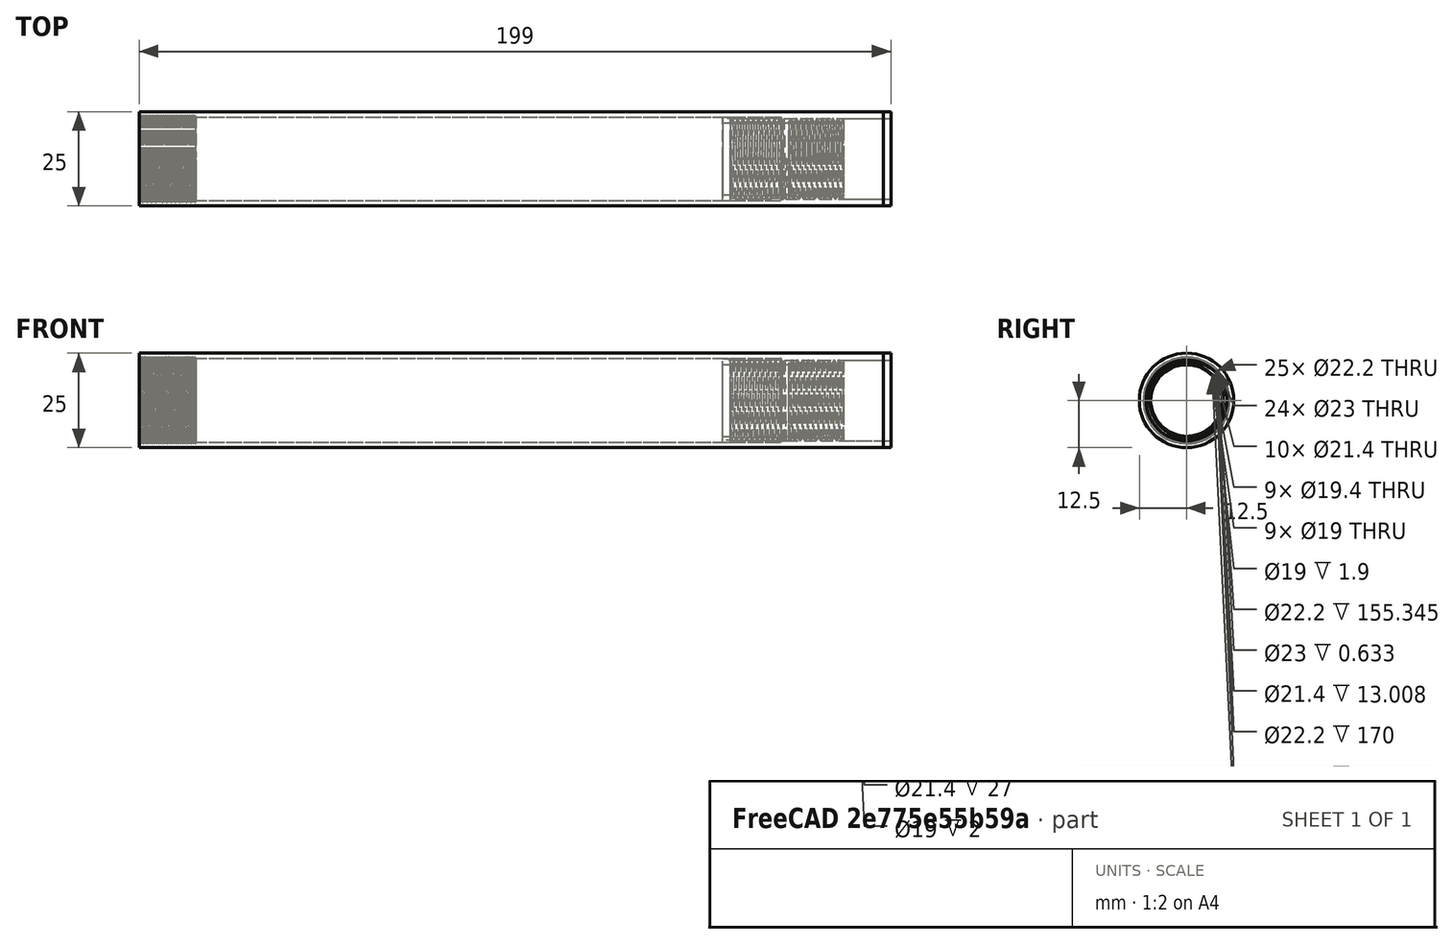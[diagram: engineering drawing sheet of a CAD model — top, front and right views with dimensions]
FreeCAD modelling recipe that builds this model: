
FCSTD DOCUMENT  (FreeCAD 0.17R13541 (Git))
Label: ERG-T-01-BH-02
License: All rights reserved
LicenseURL: http://en.wikipedia.org/wiki/All_rights_reserved
objects: Drawing::FeatureViewPython×76, Part::Cylinder×18, Part::Cut×12, Drawing::FeatureViewPart×8, Part::MultiFuse×8, Drawing::FeaturePage×4, Sketcher::SketchObject×4, Part::Helix×4, Part::Sweep×4, Part::Feature×2
note: 52 computed .brp shape members not serialized (recipe doc carries the construction recipe); baked Part::Feature solids carry a one-line shape summary decoded from their .brp

FEATURE [Drawing::FeatureViewPython] dim130  # drawing view (typed FeaturePython)
  Rotation = 0
  ViewResult = <g> \n  <line x1="95.000000" y1="103.600000" x2="95.000000" y2="144.306302" style="stroke:rgb(255,0,0);stroke-width:0.10" />\n<line x1="47.000000" y1="102.500000" x2="47.000000" y2="144.306302" style="stroke:rgb(255,0,0);stroke-width:0.10" />\n<line x1="95.000000" y1="143.306302" x2="47.000000" y2="143.306302" style="stroke:rgb(255,0,0);stroke-width:0.10" /> \n  <polygon points="47.000000,143.306302 49.000000,143.806302 49.500000,143.306302 49.000000,142.806302" style="fill:rgb(255,0,0);stroke:rgb(255,0,0);stroke-width:0" /><polygon points="95.000000,143.306302 93.000000,142.806302 92.500000,143.306302 93.000000,143.806302" style="fill:rgb(255,0,0);stroke:rgb(255,0,0);stroke-width:0" /> \n  <text x="71.000000" y="141.306302" font-family="inherit" font-size="3.6" fill="rgb(0,0,0)" text-anchor="middle" transform="rotate(0.000000 71.000000,141.306302)" >24</text> </g>
  Visible = false
  X = 0
  Y = 0
  arrowL1 = 2
  arrowL2 = 0.5
  arrowW = 1
  arrow_scheme = 0
  autoPlaceOffset = 2
  autoPlaceText = true
  click1_x = 59.2162
  click1_y = 143.306
  click2_x = 59.2162
  click2_y = 143.306
  comma_decimal_place = false
  dimension_line_overshoot = 1
  gap_datum_points = 0
  halfDimension_linear = false
  lineColor = rgb(255,0,0)
  strokeWidth = 0.1
  textFormat_linear = %(value)3.3f
  textRenderer_color = rgb(0,0,0)
  textRenderer_family = inherit
  textRenderer_size = 3.6
  unit_custom_scale = 1.7
  unit_scheme = 0
FEATURE [Drawing::FeatureViewPython] dim131  # drawing view (typed FeaturePython)
  Rotation = 0
  ViewResult = <g> \n  <line x1="95.000000" y1="103.600000" x2="95.000000" y2="144.274206" style="stroke:rgb(255,0,0);stroke-width:0.10" />\n<line x1="250.000000" y1="106.500000" x2="250.000000" y2="144.274206" style="stroke:rgb(255,0,0);stroke-width:0.10" />\n<line x1="95.000000" y1="143.274206" x2="250.000000" y2="143.274206" style="stroke:rgb(255,0,0);stroke-width:0.10" /> \n  <polygon points="250.000000,143.274206 248.000000,142.774206 247.500000,143.274206 248.000000,143.774206" style="fill:rgb(255,0,0);stroke:rgb(255,0,0);stroke-width:0" /><polygon points="95.000000,143.274206 97.000000,143.774206 97.500000,143.274206 97.000000,142.774206" style="fill:rgb(255,0,0);stroke:rgb(255,0,0);stroke-width:0" /> \n  <text x="172.500000" y="141.274206" font-family="inherit" font-size="3.6" fill="rgb(0,0,0)" text-anchor="middle" transform="rotate(0.000000 172.500000,141.274206)" >77.5</text> </g>
  Visible = false
  X = 0
  Y = 0
  arrowL1 = 2
  arrowL2 = 0.5
  arrowW = 1
  arrow_scheme = 0
  autoPlaceOffset = 2
  autoPlaceText = true
  click1_x = 247.264
  click1_y = 143.274
  click2_x = 247.264
  click2_y = 143.274
  comma_decimal_place = false
  dimension_line_overshoot = 1
  gap_datum_points = 0
  halfDimension_linear = false
  lineColor = rgb(255,0,0)
  strokeWidth = 0.1
  textFormat_linear = %(value)3.3f
  textRenderer_color = rgb(0,0,0)
  textRenderer_family = inherit
  textRenderer_size = 3.6
  unit_custom_scale = 1.7
  unit_scheme = 0
FEATURE [Drawing::FeatureViewPython] dim132  # drawing view (typed FeaturePython)
  Rotation = 0
  ViewResult = <g> \n  <line x1="95.000000" y1="100.500000" x2="95.000000" y2="91.946246" style="stroke:rgb(255,0,0);stroke-width:0.10" />\n<line x1="91.000000" y1="100.500000" x2="91.000000" y2="91.946246" style="stroke:rgb(255,0,0);stroke-width:0.10" />\n<line x1="95.000000" y1="92.946246" x2="91.000000" y2="92.946246" style="stroke:rgb(255,0,0);stroke-width:0.10" /> \n  <polygon points="91.000000,92.946246 89.000000,92.446246 88.500000,92.946246 89.000000,93.446246" style="fill:rgb(255,0,0);stroke:rgb(255,0,0);stroke-width:0" /><polygon points="95.000000,92.946246 97.000000,93.446246 97.500000,92.946246 97.000000,92.446246" style="fill:rgb(255,0,0);stroke:rgb(255,0,0);stroke-width:0" /> \n  <text x="93.000000" y="90.946246" font-family="inherit" font-size="3.6" fill="rgb(0,0,0)" text-anchor="middle" transform="rotate(0.000000 93.000000,90.946246)" >2</text> </g>
  Visible = false
  X = 0
  Y = 0
  arrowL1 = 2
  arrowL2 = 0.5
  arrowW = 1
  arrow_scheme = 0
  autoPlaceOffset = 2
  autoPlaceText = true
  click1_x = 91.8628
  click1_y = 92.9462
  click2_x = 91.8628
  click2_y = 92.9462
  comma_decimal_place = false
  dimension_line_overshoot = 1
  gap_datum_points = 0
  halfDimension_linear = false
  lineColor = rgb(255,0,0)
  strokeWidth = 0.1
  textFormat_linear = %(value)3.3f
  textRenderer_color = rgb(0,0,0)
  textRenderer_family = inherit
  textRenderer_size = 3.6
  unit_custom_scale = 1.7
  unit_scheme = 0
FEATURE [Drawing::FeatureViewPython] dim133  # drawing view (typed FeaturePython)
  Rotation = 0
  ViewResult = <g> \n  <line x1="62.208000" y1="60.500000" x2="62.208000" y2="72.297691" style="stroke:rgb(255,0,0);stroke-width:0.10" />\n<line x1="91.000000" y1="62.500000" x2="91.000000" y2="72.297691" style="stroke:rgb(255,0,0);stroke-width:0.10" />\n<line x1="62.208000" y1="71.297691" x2="91.000000" y2="71.297691" style="stroke:rgb(255,0,0);stroke-width:0.10" /> \n  <polygon points="91.000000,71.297691 89.000000,70.797691 88.500000,71.297691 89.000000,71.797691" style="fill:rgb(255,0,0);stroke:rgb(255,0,0);stroke-width:0" /><polygon points="62.208000,71.297691 64.208000,71.797691 64.708000,71.297691 64.208000,70.797691" style="fill:rgb(255,0,0);stroke:rgb(255,0,0);stroke-width:0" /> \n  <text x="76.604000" y="69.297691" font-family="inherit" font-size="3.6" fill="rgb(0,0,0)" text-anchor="middle" transform="rotate(0.000000 76.604000,69.297691)" >14.2</text> </g>
  Visible = false
  X = 0
  Y = 0
  arrowL1 = 2
  arrowL2 = 0.5
  arrowW = 1
  arrow_scheme = 0
  autoPlaceOffset = 2
  autoPlaceText = true
  click1_x = 89.6096
  click1_y = 71.2977
  click2_x = 89.6096
  click2_y = 71.2977
  comma_decimal_place = false
  dimension_line_overshoot = 1
  gap_datum_points = 0
  halfDimension_linear = false
  lineColor = rgb(255,0,0)
  strokeWidth = 0.1
  textFormat_linear = 14.2
  textRenderer_color = rgb(0,0,0)
  textRenderer_family = inherit
  textRenderer_size = 3.6
  unit_custom_scale = 1.7
  unit_scheme = 0
FEATURE [Drawing::FeatureViewPython] dim134  # drawing view (typed FeaturePython)
  Rotation = 0
  ViewResult = <g> \n  <line x1="47.000000" y1="60.500000" x2="47.000000" y2="72.294300" style="stroke:rgb(255,0,0);stroke-width:0.10" />\n<line x1="62.208000" y1="60.500000" x2="62.208000" y2="72.294300" style="stroke:rgb(255,0,0);stroke-width:0.10" />\n<line x1="47.000000" y1="71.294300" x2="62.208000" y2="71.294300" style="stroke:rgb(255,0,0);stroke-width:0.10" /> \n  <polygon points="62.208000,71.294300 60.208000,70.794300 59.708000,71.294300 60.208000,71.794300" style="fill:rgb(255,0,0);stroke:rgb(255,0,0);stroke-width:0" /><polygon points="47.000000,71.294300 49.000000,71.794300 49.500000,71.294300 49.000000,70.794300" style="fill:rgb(255,0,0);stroke:rgb(255,0,0);stroke-width:0" /> \n  <text x="54.604000" y="69.294300" font-family="inherit" font-size="3.6" fill="rgb(0,0,0)" text-anchor="middle" transform="rotate(0.000000 54.604000,69.294300)" >7.8</text> </g>
  Visible = false
  X = 0
  Y = 0
  arrowL1 = 2
  arrowL2 = 0.5
  arrowW = 1
  arrow_scheme = 0
  autoPlaceOffset = 2
  autoPlaceText = true
  click1_x = 60.9176
  click1_y = 71.2943
  click2_x = 60.9176
  click2_y = 71.2943
  comma_decimal_place = false
  dimension_line_overshoot = 1
  gap_datum_points = 0
  halfDimension_linear = false
  lineColor = rgb(255,0,0)
  strokeWidth = 0.1
  textFormat_linear = 7.8
  textRenderer_color = rgb(0,0,0)
  textRenderer_family = inherit
  textRenderer_size = 3.6
  unit_custom_scale = 1.7
  unit_scheme = 0
FEATURE [Drawing::FeatureViewPython] dim160  # drawing view (typed FeaturePython)
  Rotation = 0
  ViewResult = <g> \n  <line x1="250.000000" y1="59.400000" x2="266.991260" y2="59.400000" style="stroke:rgb(255,0,0);stroke-width:0.10" />\n<line x1="250.000000" y1="56.500000" x2="266.991260" y2="56.500000" style="stroke:rgb(255,0,0);stroke-width:0.10" />\n<line x1="265.991260" y1="59.400000" x2="265.991260" y2="56.500000" style="stroke:rgb(255,0,0);stroke-width:0.10" /> \n  <polygon points="265.991260,56.500000 266.491260,54.500000 265.991260,54.000000 265.491260,54.500000" style="fill:rgb(255,0,0);stroke:rgb(255,0,0);stroke-width:0" /><polygon points="265.991260,59.400000 265.491260,61.400000 265.991260,61.900000 266.491260,61.400000" style="fill:rgb(255,0,0);stroke:rgb(255,0,0);stroke-width:0" /> \n  <text x="263.991260" y="57.950000" font-family="inherit" font-size="3.6" fill="rgb(0,0,0)" text-anchor="middle" transform="rotate(-90.000000 263.991260,57.950000)" >1.45</text> </g>
  Visible = false
  X = 0
  Y = 0
  arrowL1 = 2
  arrowL2 = 0.5
  arrowW = 1
  arrow_scheme = 0
  autoPlaceOffset = 2
  autoPlaceText = true
  click1_x = 265.991
  click1_y = 61.2489
  click2_x = 265.991
  click2_y = 61.2489
  comma_decimal_place = false
  dimension_line_overshoot = 1
  gap_datum_points = 0
  halfDimension_linear = false
  lineColor = rgb(255,0,0)
  strokeWidth = 0.1
  textFormat_linear = %(value)3.3f
  textRenderer_color = rgb(0,0,0)
  textRenderer_family = inherit
  textRenderer_size = 3.6
  unit_custom_scale = 1.7
  unit_scheme = 0
FEATURE [Drawing::FeatureViewPython] dim161  # drawing view (typed FeaturePython)
  Rotation = 0
  ViewResult = <g> \n  <line x1="250.000000" y1="59.400000" x2="266.857529" y2="59.400000" style="stroke:rgb(255,0,0);stroke-width:0.10" />\n<line x1="250.000000" y1="103.600000" x2="266.857529" y2="103.600000" style="stroke:rgb(255,0,0);stroke-width:0.10" />\n<line x1="265.857529" y1="59.400000" x2="265.857529" y2="103.600000" style="stroke:rgb(255,0,0);stroke-width:0.10" /> \n  <polygon points="265.857529,103.600000 266.357529,101.600000 265.857529,101.100000 265.357529,101.600000" style="fill:rgb(255,0,0);stroke:rgb(255,0,0);stroke-width:0" /><polygon points="265.857529,59.400000 265.357529,61.400000 265.857529,61.900000 266.357529,61.400000" style="fill:rgb(255,0,0);stroke:rgb(255,0,0);stroke-width:0" /> \n  <text x="263.857529" y="81.500000" font-family="inherit" font-size="3.6" fill="rgb(0,0,0)" text-anchor="middle" transform="rotate(-90.000000 263.857529,81.500000)" >22.1</text> </g>
  Visible = false
  X = 0
  Y = 0
  arrowL1 = 2
  arrowL2 = 0.5
  arrowW = 1
  arrow_scheme = 0
  autoPlaceOffset = 2
  autoPlaceText = true
  click1_x = 265.858
  click1_y = 102.973
  click2_x = 265.858
  click2_y = 102.973
  comma_decimal_place = false
  dimension_line_overshoot = 1
  gap_datum_points = 0
  halfDimension_linear = false
  lineColor = rgb(255,0,0)
  strokeWidth = 0.1
  textFormat_linear = %(value)3.3f
  textRenderer_color = rgb(0,0,0)
  textRenderer_family = inherit
  textRenderer_size = 3.6
  unit_custom_scale = 1.7
  unit_scheme = 0
FEATURE [Drawing::FeatureViewPython] dim162  # drawing view (typed FeaturePython)
  Rotation = 0
  ViewResult = <g> \n  <line x1="250.000000" y1="106.500000" x2="266.857529" y2="106.500000" style="stroke:rgb(255,0,0);stroke-width:0.10" />\n<line x1="250.000000" y1="103.600000" x2="266.857529" y2="103.600000" style="stroke:rgb(255,0,0);stroke-width:0.10" />\n<line x1="265.857529" y1="106.500000" x2="265.857529" y2="103.600000" style="stroke:rgb(255,0,0);stroke-width:0.10" /> \n  <polygon points="265.857529,103.600000 266.357529,101.600000 265.857529,101.100000 265.357529,101.600000" style="fill:rgb(255,0,0);stroke:rgb(255,0,0);stroke-width:0" /><polygon points="265.857529,106.500000 265.357529,108.500000 265.857529,109.000000 266.357529,108.500000" style="fill:rgb(255,0,0);stroke:rgb(255,0,0);stroke-width:0" /> \n  <text x="263.857529" y="105.050000" font-family="inherit" font-size="3.6" fill="rgb(0,0,0)" text-anchor="middle" transform="rotate(-90.000000 263.857529,105.050000)" >1.45</text> </g>
  Visible = false
  X = 0
  Y = 0
  arrowL1 = 2
  arrowL2 = 0.5
  arrowW = 1
  arrow_scheme = 0
  autoPlaceOffset = 2
  autoPlaceText = true
  click1_x = 265.858
  click1_y = 105.915
  click2_x = 265.858
  click2_y = 105.915
  comma_decimal_place = false
  dimension_line_overshoot = 1
  gap_datum_points = 0
  halfDimension_linear = false
  lineColor = rgb(255,0,0)
  strokeWidth = 0.1
  textFormat_linear = %(value)3.3f
  textRenderer_color = rgb(0,0,0)
  textRenderer_family = inherit
  textRenderer_size = 3.6
  unit_custom_scale = 1.7
  unit_scheme = 0
FEATURE [Drawing::FeatureViewPython] dim140  # drawing view (typed FeaturePython)
  Rotation = 0
  ViewResult = <g> \n  <line x1="95.000000" y1="62.500000" x2="113.045957" y2="62.500000" style="stroke:rgb(255,0,0);stroke-width:0.10" />\n<line x1="95.000000" y1="100.500000" x2="113.045957" y2="100.500000" style="stroke:rgb(255,0,0);stroke-width:0.10" />\n<line x1="112.045957" y1="62.500000" x2="112.045957" y2="100.500000" style="stroke:rgb(255,0,0);stroke-width:0.10" /> \n  <polygon points="112.045957,100.500000 112.545957,98.500000 112.045957,98.000000 111.545957,98.500000" style="fill:rgb(255,0,0);stroke:rgb(255,0,0);stroke-width:0" /><polygon points="112.045957,62.500000 111.545957,64.500000 112.045957,65.000000 112.545957,64.500000" style="fill:rgb(255,0,0);stroke:rgb(255,0,0);stroke-width:0" /> \n  <text x="110.045957" y="81.500000" font-family="inherit" font-size="3.6" fill="rgb(0,0,0)" text-anchor="middle" transform="rotate(-90.000000 110.045957,81.500000)" >19</text> </g>
  Visible = false
  X = 0
  Y = 0
  arrowL1 = 2
  arrowL2 = 0.5
  arrowW = 1
  arrow_scheme = 0
  autoPlaceOffset = 2
  autoPlaceText = true
  click1_x = 112.046
  click1_y = 100.247
  click2_x = 112.046
  click2_y = 100.247
  comma_decimal_place = false
  dimension_line_overshoot = 1
  gap_datum_points = 0
  halfDimension_linear = false
  lineColor = rgb(255,0,0)
  strokeWidth = 0.1
  textFormat_linear = %(value)3.3f
  textRenderer_color = rgb(0,0,0)
  textRenderer_family = inherit
  textRenderer_size = 3.6
  unit_custom_scale = 1.7
  unit_scheme = 0
FEATURE [Drawing::FeatureViewPython] dim135  # drawing view (typed FeaturePython)
  Rotation = 0
  ViewResult = <g> \n  <line x1="91.000000" y1="100.500000" x2="91.000000" y2="92.012785" style="stroke:rgb(255,0,0);stroke-width:0.10" />\n<line x1="47.000000" y1="102.500000" x2="47.000000" y2="92.012785" style="stroke:rgb(255,0,0);stroke-width:0.10" />\n<line x1="91.000000" y1="93.012785" x2="47.000000" y2="93.012785" style="stroke:rgb(255,0,0);stroke-width:0.10" /> \n  <polygon points="47.000000,93.012785 49.000000,93.512785 49.500000,93.012785 49.000000,92.512785" style="fill:rgb(255,0,0);stroke:rgb(255,0,0);stroke-width:0" /><polygon points="91.000000,93.012785 89.000000,92.512785 88.500000,93.012785 89.000000,93.512785" style="fill:rgb(255,0,0);stroke:rgb(255,0,0);stroke-width:0" /> \n  <text x="69.000000" y="91.012785" font-family="inherit" font-size="3.6" fill="rgb(0,0,0)" text-anchor="middle" transform="rotate(0.000000 69.000000,91.012785)" >22</text> </g>
  Visible = false
  X = 0
  Y = 0
  arrowL1 = 2
  arrowL2 = 0.5
  arrowW = 1
  arrow_scheme = 0
  autoPlaceOffset = 2
  autoPlaceText = true
  click1_x = 47.2505
  click1_y = 93.0128
  click2_x = 47.2505
  click2_y = 93.0128
  comma_decimal_place = false
  dimension_line_overshoot = 1
  gap_datum_points = 0
  halfDimension_linear = false
  lineColor = rgb(255,0,0)
  strokeWidth = 0.1
  textFormat_linear = %(value)3.3f
  textRenderer_color = rgb(0,0,0)
  textRenderer_family = inherit
  textRenderer_size = 3.6
  unit_custom_scale = 1.7
  unit_scheme = 0
FEATURE [Drawing::FeatureViewPython] dim136  # drawing view (typed FeaturePython)
  Rotation = 0
  ViewResult = <g> \n  <line x1="47.000000" y1="60.500000" x2="41.165796" y2="60.500000" style="stroke:rgb(255,0,0);stroke-width:0.10" />\n<line x1="47.000000" y1="56.500000" x2="41.165796" y2="56.500000" style="stroke:rgb(255,0,0);stroke-width:0.10" />\n<line x1="42.165796" y1="60.500000" x2="42.165796" y2="56.500000" style="stroke:rgb(255,0,0);stroke-width:0.10" /> \n  <polygon points="42.165796,56.500000 42.665796,54.500000 42.165796,54.000000 41.665796,54.500000" style="fill:rgb(255,0,0);stroke:rgb(255,0,0);stroke-width:0" /><polygon points="42.165796,60.500000 41.665796,62.500000 42.165796,63.000000 42.665796,62.500000" style="fill:rgb(255,0,0);stroke:rgb(255,0,0);stroke-width:0" /> \n  <text x="40.165796" y="58.500000" font-family="inherit" font-size="3.6" fill="rgb(0,0,0)" text-anchor="middle" transform="rotate(-90.000000 40.165796,58.500000)" >2</text> </g>
  Visible = false
  X = 0
  Y = 0
  arrowL1 = 2
  arrowL2 = 0.5
  arrowW = 1
  arrow_scheme = 0
  autoPlaceOffset = 2
  autoPlaceText = true
  click1_x = 42.1658
  click1_y = 59.7762
  click2_x = 42.1658
  click2_y = 59.7762
  comma_decimal_place = false
  dimension_line_overshoot = 1
  gap_datum_points = 0
  halfDimension_linear = false
  lineColor = rgb(255,0,0)
  strokeWidth = 0.1
  textFormat_linear = %(value)3.3f
  textRenderer_color = rgb(0,0,0)
  textRenderer_family = inherit
  textRenderer_size = 3.6
  unit_custom_scale = 1.7
  unit_scheme = 0
FEATURE [Drawing::FeatureViewPython] dim137  # drawing view (typed FeaturePython)
  Rotation = 0
  ViewResult = <g> \n  <line x1="47.000000" y1="106.500000" x2="41.289813" y2="106.500000" style="stroke:rgb(255,0,0);stroke-width:0.10" />\n<line x1="47.000000" y1="102.500000" x2="41.289813" y2="102.500000" style="stroke:rgb(255,0,0);stroke-width:0.10" />\n<line x1="42.289813" y1="106.500000" x2="42.289813" y2="102.500000" style="stroke:rgb(255,0,0);stroke-width:0.10" /> \n  <polygon points="42.289813,102.500000 42.789813,100.500000 42.289813,100.000000 41.789813,100.500000" style="fill:rgb(255,0,0);stroke:rgb(255,0,0);stroke-width:0" /><polygon points="42.289813,106.500000 41.789813,108.500000 42.289813,109.000000 42.789813,108.500000" style="fill:rgb(255,0,0);stroke:rgb(255,0,0);stroke-width:0" /> \n  <text x="40.289813" y="104.500000" font-family="inherit" font-size="3.6" fill="rgb(0,0,0)" text-anchor="middle" transform="rotate(-90.000000 40.289813,104.500000)" >2</text> </g>
  Visible = false
  X = 0
  Y = 0
  arrowL1 = 2
  arrowL2 = 0.5
  arrowW = 1
  arrow_scheme = 0
  autoPlaceOffset = 2
  autoPlaceText = true
  click1_x = 42.2898
  click1_y = 105.042
  click2_x = 42.2898
  click2_y = 105.042
  comma_decimal_place = false
  dimension_line_overshoot = 1
  gap_datum_points = 0
  halfDimension_linear = false
  lineColor = rgb(255,0,0)
  strokeWidth = 0.1
  textFormat_linear = %(value)3.3f
  textRenderer_color = rgb(0,0,0)
  textRenderer_family = inherit
  textRenderer_size = 3.6
  unit_custom_scale = 1.7
  unit_scheme = 0
FEATURE [Drawing::FeatureViewPython] dim138  # drawing view (typed FeaturePython)
  Rotation = 0
  ViewResult = <g> \n  <line x1="47.000000" y1="60.500000" x2="41.372491" y2="60.500000" style="stroke:rgb(255,0,0);stroke-width:0.10" />\n<line x1="47.000000" y1="102.500000" x2="41.372491" y2="102.500000" style="stroke:rgb(255,0,0);stroke-width:0.10" />\n<line x1="42.372491" y1="60.500000" x2="42.372491" y2="102.500000" style="stroke:rgb(255,0,0);stroke-width:0.10" /> \n  <polygon points="42.372491,102.500000 42.872491,100.500000 42.372491,100.000000 41.872491,100.500000" style="fill:rgb(255,0,0);stroke:rgb(255,0,0);stroke-width:0" /><polygon points="42.372491,60.500000 41.872491,62.500000 42.372491,63.000000 42.872491,62.500000" style="fill:rgb(255,0,0);stroke:rgb(255,0,0);stroke-width:0" /> \n  <text x="40.372491" y="81.500000" font-family="inherit" font-size="3.6" fill="rgb(0,0,0)" text-anchor="middle" transform="rotate(-90.000000 40.372491,81.500000)" >21</text> </g>
  Visible = false
  X = 0
  Y = 0
  arrowL1 = 2
  arrowL2 = 0.5
  arrowW = 1
  arrow_scheme = 0
  autoPlaceOffset = 2
  autoPlaceText = true
  click1_x = 42.3725
  click1_y = 103.244
  click2_x = 42.3725
  click2_y = 103.244
  comma_decimal_place = false
  dimension_line_overshoot = 1
  gap_datum_points = 0
  halfDimension_linear = false
  lineColor = rgb(255,0,0)
  strokeWidth = 0.1
  textFormat_linear = %(value)3.3f
  textRenderer_color = rgb(0,0,0)
  textRenderer_family = inherit
  textRenderer_size = 3.6
  unit_custom_scale = 1.7
  unit_scheme = 0
FEATURE [Drawing::FeatureViewPython] dim139  # drawing view (typed FeaturePython)
  Rotation = 0
  ViewResult = <g> \n  <line x1="250.000000" y1="56.500000" x2="250.000000" y2="34.604582" style="stroke:rgb(255,0,0);stroke-width:0.10" />\n<line x1="47.000000" y1="56.500000" x2="47.000000" y2="34.604582" style="stroke:rgb(255,0,0);stroke-width:0.10" />\n<line x1="250.000000" y1="35.604582" x2="47.000000" y2="35.604582" style="stroke:rgb(255,0,0);stroke-width:0.10" /> \n  <polygon points="47.000000,35.604582 49.000000,36.104582 49.500000,35.604582 49.000000,35.104582" style="fill:rgb(255,0,0);stroke:rgb(255,0,0);stroke-width:0" /><polygon points="250.000000,35.604582 248.000000,35.104582 247.500000,35.604582 248.000000,36.104582" style="fill:rgb(255,0,0);stroke:rgb(255,0,0);stroke-width:0" /> \n  <text x="148.500000" y="33.604582" font-family="inherit" font-size="3.6" fill="rgb(0,0,0)" text-anchor="middle" transform="rotate(0.000000 148.500000,33.604582)" >101.5</text> </g>
  Visible = false
  X = 0
  Y = 0
  arrowL1 = 2
  arrowL2 = 0.5
  arrowW = 1
  arrow_scheme = 0
  autoPlaceOffset = 2
  autoPlaceText = true
  click1_x = 115.03
  click1_y = 35.6046
  click2_x = 115.03
  click2_y = 35.6046
  comma_decimal_place = false
  dimension_line_overshoot = 1
  gap_datum_points = 0
  halfDimension_linear = false
  lineColor = rgb(255,0,0)
  strokeWidth = 0.1
  textFormat_linear = %(value)3.3f
  textRenderer_color = rgb(0,0,0)
  textRenderer_family = inherit
  textRenderer_size = 3.6
  unit_custom_scale = 1.7
  unit_scheme = 0
FEATURE [Drawing::FeatureViewPython] dim141  # drawing view (typed FeaturePython)
  Rotation = 0
  ViewResult = <g> \n  <line x1="47.000000" y1="56.500000" x2="29.002204" y2="56.500000" style="stroke:rgb(255,0,0);stroke-width:0.10" />\n<line x1="47.000000" y1="106.500000" x2="29.002204" y2="106.500000" style="stroke:rgb(255,0,0);stroke-width:0.10" />\n<line x1="30.002204" y1="56.500000" x2="30.002204" y2="106.500000" style="stroke:rgb(255,0,0);stroke-width:0.10" /> \n  <polygon points="30.002204,106.500000 30.502204,104.500000 30.002204,104.000000 29.502204,104.500000" style="fill:rgb(255,0,0);stroke:rgb(255,0,0);stroke-width:0" /><polygon points="30.002204,56.500000 29.502204,58.500000 30.002204,59.000000 30.502204,58.500000" style="fill:rgb(255,0,0);stroke:rgb(255,0,0);stroke-width:0" /> \n  <text x="28.002204" y="81.500000" font-family="inherit" font-size="3.6" fill="rgb(0,0,0)" text-anchor="middle" transform="rotate(-90.000000 28.002204,81.500000)" >25</text> </g>
  Visible = false
  X = 0
  Y = 0
  arrowL1 = 2
  arrowL2 = 0.5
  arrowW = 1
  arrow_scheme = 0
  autoPlaceOffset = 2
  autoPlaceText = true
  click1_x = 30.0022
  click1_y = 105.651
  click2_x = 30.0022
  click2_y = 105.651
  comma_decimal_place = false
  dimension_line_overshoot = 1
  gap_datum_points = 0
  halfDimension_linear = false
  lineColor = rgb(255,0,0)
  strokeWidth = 0.1
  textFormat_linear = %(value)3.3f
  textRenderer_color = rgb(0,0,0)
  textRenderer_family = inherit
  textRenderer_size = 3.6
  unit_custom_scale = 1.7
  unit_scheme = 0
FEATURE [Drawing::FeatureViewPython] dim142  # drawing view (typed FeaturePython)
  Rotation = 0
  ViewResult = <g> \n  <line x1="95.000000" y1="62.500000" x2="112.985098" y2="62.500000" style="stroke:rgb(255,0,0);stroke-width:0.10" />\n<line x1="95.000000" y1="59.400000" x2="112.985098" y2="59.400000" style="stroke:rgb(255,0,0);stroke-width:0.10" />\n<line x1="111.985098" y1="62.500000" x2="111.985098" y2="59.400000" style="stroke:rgb(255,0,0);stroke-width:0.10" /> \n  <polygon points="111.985098,59.400000 112.485098,57.400000 111.985098,56.900000 111.485098,57.400000" style="fill:rgb(255,0,0);stroke:rgb(255,0,0);stroke-width:0" /><polygon points="111.985098,62.500000 111.485098,64.500000 111.985098,65.000000 112.485098,64.500000" style="fill:rgb(255,0,0);stroke:rgb(255,0,0);stroke-width:0" /> \n  <text x="109.985098" y="60.950000" font-family="inherit" font-size="3.6" fill="rgb(0,0,0)" text-anchor="middle" transform="rotate(-90.000000 109.985098,60.950000)" >1.55</text> </g>
  Visible = false
  X = 0
  Y = 0
  arrowL1 = 2
  arrowL2 = 0.5
  arrowW = 1
  arrow_scheme = 0
  autoPlaceOffset = 2
  autoPlaceText = true
  click1_x = 111.985
  click1_y = 67.3609
  click2_x = 111.985
  click2_y = 67.3609
  comma_decimal_place = false
  dimension_line_overshoot = 1
  gap_datum_points = 0
  halfDimension_linear = false
  lineColor = rgb(255,0,0)
  strokeWidth = 0.1
  textFormat_linear = %(value)3.3f
  textRenderer_color = rgb(0,0,0)
  textRenderer_family = inherit
  textRenderer_size = 3.6
  unit_custom_scale = 1.7
  unit_scheme = 0
FEATURE [Drawing::FeatureViewPython] dim143  # drawing view (typed FeaturePython)
  Rotation = 0
  ViewResult = <g> \n  <line x1="95.000000" y1="103.600000" x2="113.079441" y2="103.600000" style="stroke:rgb(255,0,0);stroke-width:0.10" />\n<line x1="95.000000" y1="100.500000" x2="113.079441" y2="100.500000" style="stroke:rgb(255,0,0);stroke-width:0.10" />\n<line x1="112.079441" y1="103.600000" x2="112.079441" y2="100.500000" style="stroke:rgb(255,0,0);stroke-width:0.10" /> \n  <polygon points="112.079441,100.500000 112.579441,98.500000 112.079441,98.000000 111.579441,98.500000" style="fill:rgb(255,0,0);stroke:rgb(255,0,0);stroke-width:0" /><polygon points="112.079441,103.600000 111.579441,105.600000 112.079441,106.100000 112.579441,105.600000" style="fill:rgb(255,0,0);stroke:rgb(255,0,0);stroke-width:0" /> \n  <text x="110.079441" y="102.050000" font-family="inherit" font-size="3.6" fill="rgb(0,0,0)" text-anchor="middle" transform="rotate(-90.000000 110.079441,102.050000)" >1.55</text> </g>
  Visible = false
  X = 0
  Y = 0
  arrowL1 = 2
  arrowL2 = 0.5
  arrowW = 1
  arrow_scheme = 0
  autoPlaceOffset = 2
  autoPlaceText = true
  click1_x = 112.079
  click1_y = 102.928
  click2_x = 112.079
  click2_y = 102.928
  comma_decimal_place = false
  dimension_line_overshoot = 1
  gap_datum_points = 0
  halfDimension_linear = false
  lineColor = rgb(255,0,0)
  strokeWidth = 0.1
  textFormat_linear = %(value)3.3f
  textRenderer_color = rgb(0,0,0)
  textRenderer_family = inherit
  textRenderer_size = 3.6
  unit_custom_scale = 1.7
  unit_scheme = 0
FEATURE [Drawing::FeatureViewPython] dim144  # drawing view (typed FeaturePython)
  Rotation = 0
  ViewResult = <g> \n  <line x1="63.016000" y1="102.500000" x2="56.047841" y2="102.500000" style="stroke:rgb(255,0,0);stroke-width:0.10" />\n<line x1="64.170000" y1="100.500000" x2="56.047841" y2="100.500000" style="stroke:rgb(255,0,0);stroke-width:0.10" />\n<line x1="57.047841" y1="102.500000" x2="57.047841" y2="100.500000" style="stroke:rgb(255,0,0);stroke-width:0.10" /> \n  <polygon points="57.047841,100.500000 57.547841,98.500000 57.047841,98.000000 56.547841,98.500000" style="fill:rgb(255,0,0);stroke:rgb(255,0,0);stroke-width:0" /><polygon points="57.047841,102.500000 56.547841,104.500000 57.047841,105.000000 57.547841,104.500000" style="fill:rgb(255,0,0);stroke:rgb(255,0,0);stroke-width:0" /> \n  <text x="55.047841" y="101.500000" font-family="inherit" font-size="3.6" fill="rgb(0,0,0)" text-anchor="middle" transform="rotate(-90.000000 55.047841,101.500000)" >1</text> </g>
  Visible = false
  X = 0
  Y = 0
  arrowL1 = 2
  arrowL2 = 0.5
  arrowW = 1
  arrow_scheme = 0
  autoPlaceOffset = 2
  autoPlaceText = true
  click1_x = 57.0478
  click1_y = 102.417
  click2_x = 57.0478
  click2_y = 102.417
  comma_decimal_place = false
  dimension_line_overshoot = 1
  gap_datum_points = 0
  halfDimension_linear = false
  lineColor = rgb(255,0,0)
  strokeWidth = 0.1
  textFormat_linear = %(value)3.3f
  textRenderer_color = rgb(0,0,0)
  textRenderer_family = inherit
  textRenderer_size = 3.6
  unit_custom_scale = 1.7
  unit_scheme = 0
FEATURE [Drawing::FeatureViewPython] dim146  # drawing view (typed FeaturePython)
  Rotation = 0
  ViewResult = <g> \n  <line x1="71.330000" y1="102.500000" x2="71.330000" y2="113.737333" style="stroke:rgb(255,0,0);stroke-width:0.10" />\n<line x1="74.100000" y1="102.500000" x2="74.100000" y2="113.737333" style="stroke:rgb(255,0,0);stroke-width:0.10" />\n<line x1="71.330000" y1="112.737333" x2="74.100000" y2="112.737333" style="stroke:rgb(255,0,0);stroke-width:0.10" /> \n  <polygon points="74.100000,112.737333 76.100000,113.237333 76.600000,112.737333 76.100000,112.237333" style="fill:rgb(255,0,0);stroke:rgb(255,0,0);stroke-width:0" /><polygon points="71.330000,112.737333 69.330000,112.237333 68.830000,112.737333 69.330000,113.237333" style="fill:rgb(255,0,0);stroke:rgb(255,0,0);stroke-width:0" /> \n  <text x="72.715000" y="110.737333" font-family="inherit" font-size="3.6" fill="rgb(0,0,0)" text-anchor="middle" transform="rotate(0.000000 72.715000,110.737333)" >1.4</text> </g>
  Visible = false
  X = 0
  Y = 0
  arrowL1 = 2
  arrowL2 = 0.5
  arrowW = 1
  arrow_scheme = 0
  autoPlaceOffset = 2
  autoPlaceText = true
  click1_x = 74.5203
  click1_y = 112.737
  click2_x = 74.5203
  click2_y = 112.737
  comma_decimal_place = false
  dimension_line_overshoot = 1
  gap_datum_points = 0
  halfDimension_linear = false
  lineColor = rgb(255,0,0)
  strokeWidth = 0.1
  textFormat_linear = %(value)3.1f
  textRenderer_color = rgb(0,0,0)
  textRenderer_family = inherit
  textRenderer_size = 3.6
  unit_custom_scale = 1.7
  unit_scheme = 0
FEATURE [Part::Feature] Fusion003_cs003
  shape: bbox 101.5 x 6.566e-05 x 25 mm, 0 faces, 0 solids (baked)
FEATURE [Drawing::FeatureViewPart] Ortho019  label="Ortho_0_009"
  Direction = (0,1,0)
  HiddenWidth = 0.15
  LineWidth = 0.35
  Rotation = -90
  Scale = 2
  ShowHiddenLines = false
  ShowSmoothLines = false
  Source = -> Fusion003_cs003
  Tolerance = 0.05
  ViewResult = <blob: 5370 chars omitted>
  Visible = false
  X = 406
  Y = 81.5
FEATURE [Drawing::FeaturePage] Page008  label="BatteryHolder2-CS"
  EditableTexts = Dr. Zoidberg | 05.02.2019 | x2.0 | unknown | ERG-T-01 | Battery Holder. Cross Section. | 03 | 03
  Group = -> [Ortho019,dim130,dim131,dim132,dim133,dim134,dim135,dim136,dim137,dim138,dim139,dim141,dim142,dim143,dim144,dim146,dim160,dim161,dim162,dim140]
  Template = <path>//share/freecad/Mod/Drawing/Templates/A4_Landscape.svg
FEATURE [Sketcher::SketchObject] Sketch007  label="T006"
  Placement = pos=(157,0,-10.6) rot=(1,0,0;1.5708rad)
  sketch-geometry (3):
    g0: LineSegment StartX=0.00120621 StartY=1.19996 StartZ=0 EndX=-0.691594 EndY=0 EndZ=0
    g1: LineSegment StartX=0.694006 StartY=0 StartZ=0 EndX=0.00120621 EndY=1.19996 EndZ=0
    g2: LineSegment StartX=-0.691594 StartY=0 StartZ=0 EndX=0.694006 EndY=0 EndZ=0
  constraints (8):
    c: PointOnObject(g1,g-1)
    c: Coincident(g1,g0)
    c: Coincident(g2,g0)
    c: Coincident(g2,g1)
    c: Horizontal(g2)
    c: Angle(g2,g0) = 1.0472
    c: Angle(g1,g2) = 1.0472
    c: Distance(g0,g0) = 1.3856
FEATURE [Drawing::FeatureViewPython] dim151  # drawing view (typed FeaturePython)
  Rotation = 0
  ViewResult = <g> \n  <line x1="79.250000" y1="71.068300" x2="88.425527" y2="71.068300" style="stroke:rgb(255,0,0);stroke-width:0.10" />\n<line x1="79.250000" y1="70.800000" x2="88.425527" y2="70.800000" style="stroke:rgb(255,0,0);stroke-width:0.10" />\n<line x1="87.425527" y1="71.068300" x2="87.425527" y2="70.800000" style="stroke:rgb(255,0,0);stroke-width:0.10" /> \n  <polygon points="87.425527,70.800000 87.925527,68.800000 87.425527,68.300000 86.925527,68.800000" style="fill:rgb(255,0,0);stroke:rgb(255,0,0);stroke-width:0" /><polygon points="87.425527,71.068300 86.925527,73.068300 87.425527,73.568300 87.925527,73.068300" style="fill:rgb(255,0,0);stroke:rgb(255,0,0);stroke-width:0" /> \n  <text x="85.425527" y="70.934150" font-family="inherit" font-size="3.6" fill="rgb(0,0,0)" text-anchor="middle" transform="rotate(-90.000000 85.425527,70.934150)" >7.8</text> </g>
  Visible = false
  X = 0
  Y = 0
  arrowL1 = 2
  arrowL2 = 0.5
  arrowW = 1
  arrow_scheme = 0
  autoPlaceOffset = 2
  autoPlaceText = true
  click1_x = 87.4255
  click1_y = 62.8155
  click2_x = 87.4255
  click2_y = 62.8155
  comma_decimal_place = false
  dimension_line_overshoot = 1
  gap_datum_points = 0
  halfDimension_linear = false
  lineColor = rgb(255,0,0)
  strokeWidth = 0.1
  textFormat_linear = 7.8
  textRenderer_color = rgb(0,0,0)
  textRenderer_family = inherit
  textRenderer_size = 3.6
  unit_custom_scale = 1.7
  unit_scheme = 0
FEATURE [Drawing::FeatureViewPython] dim155  # drawing view (typed FeaturePython)
  Rotation = 0
  ViewResult = <g> \n  <line x1="121.750000" y1="91.864355" x2="121.750000" y2="110.680676" style="stroke:rgb(255,0,0);stroke-width:0.10" />\n<line x1="79.250000" y1="92.017495" x2="79.250000" y2="110.680676" style="stroke:rgb(255,0,0);stroke-width:0.10" />\n<line x1="121.750000" y1="109.680676" x2="79.250000" y2="109.680676" style="stroke:rgb(255,0,0);stroke-width:0.10" /> \n  <polygon points="79.250000,109.680676 81.250000,110.180676 81.750000,109.680676 81.250000,109.180676" style="fill:rgb(255,0,0);stroke:rgb(255,0,0);stroke-width:0" /><polygon points="121.750000,109.680676 119.750000,109.180676 119.250000,109.680676 119.750000,110.180676" style="fill:rgb(255,0,0);stroke:rgb(255,0,0);stroke-width:0" /> \n  <text x="100.500000" y="107.680676" font-family="inherit" font-size="3.6" fill="rgb(0,0,0)" text-anchor="middle" transform="rotate(0.000000 100.500000,107.680676)" >42.5</text> </g>
  Visible = false
  X = 0
  Y = 0
  arrowL1 = 2
  arrowL2 = 0.5
  arrowW = 1
  arrow_scheme = 0
  autoPlaceOffset = 2
  autoPlaceText = true
  click1_x = 89.9858
  click1_y = 109.681
  click2_x = 89.9858
  click2_y = 109.681
  comma_decimal_place = false
  dimension_line_overshoot = 1
  gap_datum_points = 0
  halfDimension_linear = false
  lineColor = rgb(255,0,0)
  strokeWidth = 0.1
  textFormat_linear = %(value)3.3f
  textRenderer_color = rgb(0,0,0)
  textRenderer_family = inherit
  textRenderer_size = 3.6
  unit_custom_scale = 1.7
  unit_scheme = 0
FEATURE [Drawing::FeatureViewPython] dim152  # drawing view (typed FeaturePython)
  Rotation = 0
  ViewResult = <g> \n  <line x1="276.250000" y1="70.400000" x2="291.491018" y2="70.400000" style="stroke:rgb(255,0,0);stroke-width:0.10" />\n<line x1="276.250000" y1="92.600000" x2="291.491018" y2="92.600000" style="stroke:rgb(255,0,0);stroke-width:0.10" />\n<line x1="290.491018" y1="70.400000" x2="290.491018" y2="92.600000" style="stroke:rgb(255,0,0);stroke-width:0.10" /> \n  <polygon points="290.491018,92.600000 290.991018,90.600000 290.491018,90.100000 289.991018,90.600000" style="fill:rgb(255,0,0);stroke:rgb(255,0,0);stroke-width:0" /><polygon points="290.491018,70.400000 289.991018,72.400000 290.491018,72.900000 290.991018,72.400000" style="fill:rgb(255,0,0);stroke:rgb(255,0,0);stroke-width:0" /> \n  <text x="288.491018" y="81.500000" font-family="inherit" font-size="3.6" fill="rgb(0,0,0)" text-anchor="middle" transform="rotate(-90.000000 288.491018,81.500000)" >22.2</text> </g>
  Visible = false
  X = 0
  Y = 0
  arrowL1 = 2
  arrowL2 = 0.5
  arrowW = 1
  arrow_scheme = 0
  autoPlaceOffset = 2
  autoPlaceText = true
  click1_x = 290.491
  click1_y = 92.439
  click2_x = 290.491
  click2_y = 92.439
  comma_decimal_place = false
  dimension_line_overshoot = 1
  gap_datum_points = 0
  halfDimension_linear = false
  lineColor = rgb(255,0,0)
  strokeWidth = 0.1
  textFormat_linear = %(value)3.3f
  textRenderer_color = rgb(0,0,0)
  textRenderer_family = inherit
  textRenderer_size = 3.6
  unit_custom_scale = 1.7
  unit_scheme = 0
FEATURE [Drawing::FeatureViewPython] dim153  # drawing view (typed FeaturePython)
  Rotation = 0
  ViewResult = <g> \n  <line x1="276.250000" y1="69.000000" x2="291.491018" y2="69.000000" style="stroke:rgb(255,0,0);stroke-width:0.10" />\n<line x1="276.250000" y1="70.400000" x2="291.491018" y2="70.400000" style="stroke:rgb(255,0,0);stroke-width:0.10" />\n<line x1="290.491018" y1="69.000000" x2="290.491018" y2="70.400000" style="stroke:rgb(255,0,0);stroke-width:0.10" /> \n  <polygon points="290.491018,70.400000 289.991018,72.400000 290.491018,72.900000 290.991018,72.400000" style="fill:rgb(255,0,0);stroke:rgb(255,0,0);stroke-width:0" /><polygon points="290.491018,69.000000 290.991018,67.000000 290.491018,66.500000 289.991018,67.000000" style="fill:rgb(255,0,0);stroke:rgb(255,0,0);stroke-width:0" /> \n  <text x="288.491018" y="69.700000" font-family="inherit" font-size="3.6" fill="rgb(0,0,0)" text-anchor="middle" transform="rotate(-90.000000 288.491018,69.700000)" >1.4</text> </g>
  Visible = false
  X = 0
  Y = 0
  arrowL1 = 2
  arrowL2 = 0.5
  arrowW = 1
  arrow_scheme = 0
  autoPlaceOffset = 2
  autoPlaceText = true
  click1_x = 290.491
  click1_y = 72.2013
  click2_x = 290.491
  click2_y = 72.2013
  comma_decimal_place = false
  dimension_line_overshoot = 1
  gap_datum_points = 0
  halfDimension_linear = false
  lineColor = rgb(255,0,0)
  strokeWidth = 0.1
  textFormat_linear = %(value)3.3f
  textRenderer_color = rgb(0,0,0)
  textRenderer_family = inherit
  textRenderer_size = 3.6
  unit_custom_scale = 1.7
  unit_scheme = 0
FEATURE [Drawing::FeatureViewPython] dim154  # drawing view (typed FeaturePython)
  Rotation = 0
  ViewResult = <g> \n  <line x1="276.250000" y1="92.600000" x2="291.528489" y2="92.600000" style="stroke:rgb(255,0,0);stroke-width:0.10" />\n<line x1="276.250000" y1="94.000000" x2="291.528489" y2="94.000000" style="stroke:rgb(255,0,0);stroke-width:0.10" />\n<line x1="290.528489" y1="92.600000" x2="290.528489" y2="94.000000" style="stroke:rgb(255,0,0);stroke-width:0.10" /> \n  <polygon points="290.528489,94.000000 290.028489,96.000000 290.528489,96.500000 291.028489,96.000000" style="fill:rgb(255,0,0);stroke:rgb(255,0,0);stroke-width:0" /><polygon points="290.528489,92.600000 291.028489,90.600000 290.528489,90.100000 290.028489,90.600000" style="fill:rgb(255,0,0);stroke:rgb(255,0,0);stroke-width:0" /> \n  <text x="288.528489" y="93.300000" font-family="inherit" font-size="3.6" fill="rgb(0,0,0)" text-anchor="middle" transform="rotate(-90.000000 288.528489,93.300000)" >1.4</text> </g>
  Visible = false
  X = 0
  Y = 0
  arrowL1 = 2
  arrowL2 = 0.5
  arrowW = 1
  arrow_scheme = 0
  autoPlaceOffset = 2
  autoPlaceText = true
  click1_x = 290.528
  click1_y = 94.4593
  click2_x = 290.528
  click2_y = 94.4593
  comma_decimal_place = false
  dimension_line_overshoot = 1
  gap_datum_points = 0
  halfDimension_linear = false
  lineColor = rgb(255,0,0)
  strokeWidth = 0.1
  textFormat_linear = %(value)3.3f
  textRenderer_color = rgb(0,0,0)
  textRenderer_family = inherit
  textRenderer_size = 3.6
  unit_custom_scale = 1.7
  unit_scheme = 0
FEATURE [Drawing::FeatureViewPython] dim156  # drawing view (typed FeaturePython)
  Rotation = 0
  ViewResult = <g> \n  <line x1="79.250000" y1="70.982505" x2="57.858456" y2="70.982505" style="stroke:rgb(255,0,0);stroke-width:0.10" />\n<line x1="79.250000" y1="92.017495" x2="57.858456" y2="92.017495" style="stroke:rgb(255,0,0);stroke-width:0.10" />\n<line x1="58.858456" y1="70.982505" x2="58.858456" y2="92.017495" style="stroke:rgb(255,0,0);stroke-width:0.10" /> \n  <polygon points="58.858456,92.017495 59.358456,90.017495 58.858456,89.517495 58.358456,90.017495" style="fill:rgb(255,0,0);stroke:rgb(255,0,0);stroke-width:0" /><polygon points="58.858456,70.982505 58.358456,72.982505 58.858456,73.482505 59.358456,72.982505" style="fill:rgb(255,0,0);stroke:rgb(255,0,0);stroke-width:0" /> \n  <text x="56.858456" y="81.500000" font-family="inherit" font-size="3.6" fill="rgb(0,0,0)" text-anchor="middle" transform="rotate(-90.000000 56.858456,81.500000)" >21.035</text> </g>
  Visible = false
  X = 0
  Y = 0
  arrowL1 = 2
  arrowL2 = 0.5
  arrowW = 1
  arrow_scheme = 0
  autoPlaceOffset = 2
  autoPlaceText = true
  click1_x = 58.8585
  click1_y = 91.4088
  click2_x = 58.8585
  click2_y = 91.4088
  comma_decimal_place = false
  dimension_line_overshoot = 1
  gap_datum_points = 0
  halfDimension_linear = false
  lineColor = rgb(255,0,0)
  strokeWidth = 0.1
  textFormat_linear = %(value)3.3f
  textRenderer_color = rgb(0,0,0)
  textRenderer_family = inherit
  textRenderer_size = 3.6
  unit_custom_scale = 1.7
  unit_scheme = 0
FEATURE [Drawing::FeatureViewPython] dim157  # drawing view (typed FeaturePython)
  Rotation = 0
  ViewResult = <g> \n  <line x1="105.688000" y1="71.606020" x2="72.268110" y2="71.606020" style="stroke:rgb(255,0,0);stroke-width:0.10" />\n<line x1="105.096000" y1="91.001010" x2="72.268110" y2="91.001010" style="stroke:rgb(255,0,0);stroke-width:0.10" />\n<line x1="73.268110" y1="71.606020" x2="73.268110" y2="91.001010" style="stroke:rgb(255,0,0);stroke-width:0.10" /> \n  <polygon points="73.268110,91.001010 73.768110,89.001010 73.268110,88.501010 72.768110,89.001010" style="fill:rgb(255,0,0);stroke:rgb(255,0,0);stroke-width:0" /><polygon points="73.268110,71.606020 72.768110,73.606020 73.268110,74.106020 73.768110,73.606020" style="fill:rgb(255,0,0);stroke:rgb(255,0,0);stroke-width:0" /> \n  <text x="71.268110" y="81.303515" font-family="inherit" font-size="3.6" fill="rgb(0,0,0)" text-anchor="middle" transform="rotate(-90.000000 71.268110,81.303515)" >19.4</text> </g>
  Visible = false
  X = 0
  Y = 0
  arrowL1 = 2
  arrowL2 = 0.5
  arrowW = 1
  arrow_scheme = 0
  autoPlaceOffset = 2
  autoPlaceText = true
  click1_x = 73.2681
  click1_y = 89.9581
  click2_x = 73.2681
  click2_y = 89.9581
  comma_decimal_place = false
  dimension_line_overshoot = 1
  gap_datum_points = 0
  halfDimension_linear = false
  lineColor = rgb(255,0,0)
  strokeWidth = 0.1
  textFormat_linear = %(value)3.1f
  textRenderer_color = rgb(0,0,0)
  textRenderer_family = inherit
  textRenderer_size = 3.6
  unit_custom_scale = 1.7
  unit_scheme = 0
FEATURE [Drawing::FeatureViewPython] dia026  # drawing view (typed FeaturePython)
  Rotation = 0
  ViewResult = <g>  <circle cx ="53.875000" cy ="81.500000" r="0.250000" stroke="none" fill="rgb(255,0,0)" /> \n<line x1="35.510421" y1="129.384504" x2="58.351081" y2="69.828895" style="stroke:rgb(255,0,0);stroke-width:0.10" />\n<polygon points="49.398919,93.171105 50.581936,91.482772 50.294135,90.836884 49.648248,91.124685" style="fill:rgb(255,0,0);stroke:rgb(255,0,0);stroke-width:0" />\n<polygon points="58.351081,69.828895 57.168064,71.517228 57.455865,72.163116 58.101752,71.875315" style="fill:rgb(255,0,0);stroke:rgb(255,0,0);stroke-width:0" />\n<line x1="35.510421" y1="129.384504" x2="26.193330" y2="129.384504" style="stroke:rgb(255,0,0);stroke-width:0.10" />\n<text x="30.851876" y="127.384504" font-family="inherit" font-size="3.6" fill="rgb(0,0,0)" text-anchor="middle" transform="rotate(0.000000 30.851876,127.384504)" >Ø25</text> </g>
  Visible = false
  X = 0
  Y = 0
  arrowL1 = 2
  arrowL2 = 0.5
  arrowW = 1
  arrow_scheme = 0
  autoPlaceOffset = 2
  autoPlaceText = true
  centerPointDia = 0.5
  click1_x = 35.5104
  click1_y = 129.385
  click2_x = 26.1933
  click2_y = 130.439
  click3_x = 26.1933
  click3_y = 130.439
  comma_decimal_place = false
  lineColor = rgb(255,0,0)
  strokeWidth = 0.1
  textFormat_circular = Ø%(value)3.3f
  textRenderer_color = rgb(0,0,0)
  textRenderer_family = inherit
  textRenderer_size = 3.6
  unit_custom_scale = 1.7
  unit_scheme = 0
FEATURE [Drawing::FeatureViewPython] dia024  # drawing view (typed FeaturePython)
  Rotation = 0
  ViewResult = <g>  <circle cx ="243.125000" cy ="81.500000" r="0.250000" stroke="none" fill="rgb(255,0,0)" /> \n<line x1="259.438433" y1="97.490009" x2="236.340569" y2="74.850075" style="stroke:rgb(255,0,0);stroke-width:0.10" />\n<polygon points="249.909431,88.149925 248.831125,86.392865 248.124054,86.399945 248.131133,87.107016" style="fill:rgb(255,0,0);stroke:rgb(255,0,0);stroke-width:0" />\n<polygon points="236.340569,74.850075 237.418875,76.607135 238.125946,76.600055 238.118867,75.892984" style="fill:rgb(255,0,0);stroke:rgb(255,0,0);stroke-width:0" />\n<line x1="259.438433" y1="97.490009" x2="280.166762" y2="97.490009" style="stroke:rgb(255,0,0);stroke-width:0.10" />\n<text x="269.802598" y="95.490009" font-family="inherit" font-size="3.6" fill="rgb(0,0,0)" text-anchor="middle" transform="rotate(0.000000 269.802598,95.490009)" >Ø19</text> </g>
  Visible = false
  X = 0
  Y = 0
  arrowL1 = 2
  arrowL2 = 0.5
  arrowW = 1
  arrow_scheme = 0
  autoPlaceOffset = 2
  autoPlaceText = true
  centerPointDia = 0.5
  click1_x = 259.438
  click1_y = 97.49
  click2_x = 280.167
  click2_y = 102.572
  click3_x = 280.167
  click3_y = 102.572
  comma_decimal_place = false
  lineColor = rgb(255,0,0)
  strokeWidth = 0.1
  textFormat_circular = Ø%(value)3.3f
  textRenderer_color = rgb(0,0,0)
  textRenderer_family = inherit
  textRenderer_size = 3.6
  unit_custom_scale = 1.7
  unit_scheme = 0
FEATURE [Drawing::FeatureViewPython] dia025  # drawing view (typed FeaturePython)
  Rotation = 0
  ViewResult = <g>  <circle cx ="53.875000" cy ="81.500000" r="0.250000" stroke="none" fill="rgb(255,0,0)" /> \n<line x1="29.364657" y1="113.661474" x2="61.451785" y2="71.558052" style="stroke:rgb(255,0,0);stroke-width:0.10" />\n<polygon points="46.298215,91.441948 47.908179,90.154308 47.813572,89.453559 47.112823,89.548165" style="fill:rgb(255,0,0);stroke:rgb(255,0,0);stroke-width:0" />\n<polygon points="61.451785,71.558052 59.841821,72.845692 59.936428,73.546441 60.637177,73.451835" style="fill:rgb(255,0,0);stroke:rgb(255,0,0);stroke-width:0" />\n<line x1="29.364657" y1="113.661474" x2="16.201190" y2="113.661474" style="stroke:rgb(255,0,0);stroke-width:0.10" />\n<text x="22.782924" y="111.661474" font-family="inherit" font-size="3.6" fill="rgb(0,0,0)" text-anchor="middle" transform="rotate(0.000000 22.782924,111.661474)" >Ø25</text> </g>
  Visible = false
  X = 0
  Y = 0
  arrowL1 = 2
  arrowL2 = 0.5
  arrowW = 1
  arrow_scheme = 0
  autoPlaceOffset = 2
  autoPlaceText = true
  centerPointDia = 0.5
  click1_x = 29.3647
  click1_y = 113.661
  click2_x = 16.2012
  click2_y = 116.446
  click3_x = 16.2012
  click3_y = 116.446
  comma_decimal_place = false
  lineColor = rgb(255,0,0)
  strokeWidth = 0.1
  textFormat_circular = Ø%(value)3.3f
  textRenderer_color = rgb(0,0,0)
  textRenderer_family = inherit
  textRenderer_size = 3.6
  unit_custom_scale = 1.7
  unit_scheme = 0
FEATURE [Drawing::FeatureViewPython] dim145  # drawing view (typed FeaturePython)
  Rotation = 0
  ViewResult = <g> \n  <line x1="276.250000" y1="69.000000" x2="276.250000" y2="35.952252" style="stroke:rgb(255,0,0);stroke-width:0.10" />\n<line x1="79.250000" y1="69.000000" x2="79.250000" y2="35.952252" style="stroke:rgb(255,0,0);stroke-width:0.10" />\n<line x1="276.250000" y1="36.952252" x2="79.250000" y2="36.952252" style="stroke:rgb(255,0,0);stroke-width:0.10" /> \n  <polygon points="79.250000,36.952252 81.250000,37.452252 81.750000,36.952252 81.250000,36.452252" style="fill:rgb(255,0,0);stroke:rgb(255,0,0);stroke-width:0" /><polygon points="276.250000,36.952252 274.250000,36.452252 273.750000,36.952252 274.250000,37.452252" style="fill:rgb(255,0,0);stroke:rgb(255,0,0);stroke-width:0" /> \n  <text x="177.750000" y="34.952252" font-family="inherit" font-size="3.6" fill="rgb(0,0,0)" text-anchor="middle" transform="rotate(0.000000 177.750000,34.952252)" >197</text> </g>
  Visible = false
  X = 0
  Y = 0
  arrowL1 = 2
  arrowL2 = 0.5
  arrowW = 1
  arrow_scheme = 0
  autoPlaceOffset = 2
  autoPlaceText = true
  click1_x = 206.468
  click1_y = 36.9523
  click2_x = 206.468
  click2_y = 36.9523
  comma_decimal_place = false
  dimension_line_overshoot = 1
  gap_datum_points = 0
  halfDimension_linear = false
  lineColor = rgb(255,0,0)
  strokeWidth = 0.1
  textFormat_linear = %(value)3.3f
  textRenderer_color = rgb(0,0,0)
  textRenderer_family = inherit
  textRenderer_size = 3.6
  unit_custom_scale = 1.7
  unit_scheme = 0
FEATURE [Drawing::FeatureViewPython] dim147  # drawing view (typed FeaturePython)
  Rotation = 0
  ViewResult = <g> \n  <line x1="276.250000" y1="70.678300" x2="187.538004" y2="70.678300" style="stroke:rgb(255,0,0);stroke-width:0.10" />\n<line x1="276.250000" y1="70.400000" x2="187.538004" y2="70.400000" style="stroke:rgb(255,0,0);stroke-width:0.10" />\n<line x1="188.538004" y1="70.678300" x2="188.538004" y2="70.400000" style="stroke:rgb(255,0,0);stroke-width:0.10" /> \n  <polygon points="188.538004,70.400000 189.038004,68.400000 188.538004,67.900000 188.038004,68.400000" style="fill:rgb(255,0,0);stroke:rgb(255,0,0);stroke-width:0" /><polygon points="188.538004,70.678300 188.038004,72.678300 188.538004,73.178300 189.038004,72.678300" style="fill:rgb(255,0,0);stroke:rgb(255,0,0);stroke-width:0" /> \n  <text x="186.538004" y="70.539150" font-family="inherit" font-size="3.6" fill="rgb(0,0,0)" text-anchor="middle" transform="rotate(-90.000000 186.538004,70.539150)" >0.278</text> </g>
  Visible = false
  X = 0
  Y = 0
  arrowL1 = 2
  arrowL2 = 0.5
  arrowW = 1
  arrow_scheme = 0
  autoPlaceOffset = 2
  autoPlaceText = true
  click1_x = 188.538
  click1_y = 44.8318
  click2_x = 188.538
  click2_y = 44.8318
  comma_decimal_place = false
  dimension_line_overshoot = 1
  gap_datum_points = 0
  halfDimension_linear = false
  lineColor = rgb(255,0,0)
  strokeWidth = 0.1
  textFormat_linear = %(value)3.3f
  textRenderer_color = rgb(0,0,0)
  textRenderer_family = inherit
  textRenderer_size = 3.6
  unit_custom_scale = 1.7
  unit_scheme = 0
FEATURE [Drawing::FeatureViewPython] dim148  # drawing view (typed FeaturePython)
  Rotation = 0
  ViewResult = <g> \n  <line x1="121.750000" y1="70.450000" x2="121.750000" y2="43.855703" style="stroke:rgb(255,0,0);stroke-width:0.10" />\n<line x1="79.250000" y1="70.982505" x2="79.250000" y2="43.855703" style="stroke:rgb(255,0,0);stroke-width:0.10" />\n<line x1="121.750000" y1="44.855703" x2="79.250000" y2="44.855703" style="stroke:rgb(255,0,0);stroke-width:0.10" /> \n  <polygon points="79.250000,44.855703 81.250000,45.355703 81.750000,44.855703 81.250000,44.355703" style="fill:rgb(255,0,0);stroke:rgb(255,0,0);stroke-width:0" /><polygon points="121.750000,44.855703 119.750000,44.355703 119.250000,44.855703 119.750000,45.355703" style="fill:rgb(255,0,0);stroke:rgb(255,0,0);stroke-width:0" /> \n  <text x="100.500000" y="42.855703" font-family="inherit" font-size="3.6" fill="rgb(0,0,0)" text-anchor="middle" transform="rotate(0.000000 100.500000,42.855703)" >42.5</text> </g>
  Visible = false
  X = 0
  Y = 0
  arrowL1 = 2
  arrowL2 = 0.5
  arrowW = 1
  arrow_scheme = 0
  autoPlaceOffset = 2
  autoPlaceText = true
  click1_x = 91.3679
  click1_y = 44.8557
  click2_x = 91.3679
  click2_y = 44.8557
  comma_decimal_place = false
  dimension_line_overshoot = 1
  gap_datum_points = 0
  halfDimension_linear = false
  lineColor = rgb(255,0,0)
  strokeWidth = 0.1
  textFormat_linear = %(value)3.3f
  textRenderer_color = rgb(0,0,0)
  textRenderer_family = inherit
  textRenderer_size = 3.6
  unit_custom_scale = 1.7
  unit_scheme = 0
FEATURE [Drawing::FeatureViewPython] dim149  # drawing view (typed FeaturePython)
  Rotation = 0
  ViewResult = <g> \n  <line x1="121.750000" y1="72.238180" x2="125.659532" y2="72.238180" style="stroke:rgb(255,0,0);stroke-width:0.10" />\n<line x1="121.750000" y1="72.000000" x2="125.659532" y2="72.000000" style="stroke:rgb(255,0,0);stroke-width:0.10" />\n<line x1="124.659532" y1="72.238180" x2="124.659532" y2="72.000000" style="stroke:rgb(255,0,0);stroke-width:0.10" /> \n  <polygon points="124.659532,72.000000 125.159532,70.000000 124.659532,69.500000 124.159532,70.000000" style="fill:rgb(255,0,0);stroke:rgb(255,0,0);stroke-width:0" /><polygon points="124.659532,72.238180 124.159532,74.238180 124.659532,74.738180 125.159532,74.238180" style="fill:rgb(255,0,0);stroke:rgb(255,0,0);stroke-width:0" /> \n  <text x="122.659532" y="72.119090" font-family="inherit" font-size="3.6" fill="rgb(0,0,0)" text-anchor="middle" transform="rotate(-90.000000 122.659532,72.119090)" >0.238</text> </g>
  Visible = false
  X = 0
  Y = 0
  arrowL1 = 2
  arrowL2 = 0.5
  arrowW = 1
  arrow_scheme = 0
  autoPlaceOffset = 2
  autoPlaceText = true
  click1_x = 124.66
  click1_y = 62.7262
  click2_x = 124.66
  click2_y = 62.7262
  comma_decimal_place = false
  dimension_line_overshoot = 1
  gap_datum_points = 0
  halfDimension_linear = false
  lineColor = rgb(255,0,0)
  strokeWidth = 0.1
  textFormat_linear = %(value)3.3f
  textRenderer_color = rgb(0,0,0)
  textRenderer_family = inherit
  textRenderer_size = 3.6
  unit_custom_scale = 1.7
  unit_scheme = 0
FEATURE [Drawing::FeatureViewPython] dim150  # drawing view (typed FeaturePython)
  Rotation = 0
  ViewResult = <g> \n  <line x1="121.750000" y1="71.544290" x2="121.750000" y2="61.779797" style="stroke:rgb(255,0,0);stroke-width:0.10" />\n<line x1="92.244000" y1="70.800000" x2="92.244000" y2="61.779797" style="stroke:rgb(255,0,0);stroke-width:0.10" />\n<line x1="121.750000" y1="62.779797" x2="92.244000" y2="62.779797" style="stroke:rgb(255,0,0);stroke-width:0.10" /> \n  <polygon points="92.244000,62.779797 94.244000,63.279797 94.744000,62.779797 94.244000,62.279797" style="fill:rgb(255,0,0);stroke:rgb(255,0,0);stroke-width:0" /><polygon points="121.750000,62.779797 119.750000,62.279797 119.250000,62.779797 119.750000,63.279797" style="fill:rgb(255,0,0);stroke:rgb(255,0,0);stroke-width:0" /> \n  <text x="106.997000" y="60.779797" font-family="inherit" font-size="3.6" fill="rgb(0,0,0)" text-anchor="middle" transform="rotate(0.000000 106.997000,60.779797)" >14.2</text> </g>
  Visible = false
  X = 0
  Y = 0
  arrowL1 = 2
  arrowL2 = 0.5
  arrowW = 1
  arrow_scheme = 0
  autoPlaceOffset = 2
  autoPlaceText = true
  click1_x = 95.1438
  click1_y = 62.7798
  click2_x = 95.1438
  click2_y = 62.7798
  comma_decimal_place = false
  dimension_line_overshoot = 1
  gap_datum_points = 0
  halfDimension_linear = false
  lineColor = rgb(255,0,0)
  strokeWidth = 0.1
  textFormat_linear = 14.2
  textRenderer_color = rgb(0,0,0)
  textRenderer_family = inherit
  textRenderer_size = 3.6
  unit_custom_scale = 1.7
  unit_scheme = 0
FEATURE [Part::Cylinder] Cylinder004  label="Cylinder002"
  Angle = 360
  AttacherType = Attacher::AttachEngine3D
  Height = 27
  Placement = pos=(171,0,0) rot=(0,1,0;1.5708rad)
  Radius = 10.7
FEATURE [Part::Helix] Helix010
  Angle = 35.82
  AttacherType = Attacher::AttachEngine3D
  Height = 1.3856
  LocalCoord = 0
  Pitch = 1.3856
  Placement = pos=(170.856,0,0) rot=(0,1,0;1.5708rad)
  Radius = 9.5
  Style = 1
FEATURE [Part::Cylinder] Cylinder003  label="Cylinder001"
  Angle = 360
  AttacherType = Attacher::AttachEngine3D
  Height = 170
  Placement = pos=(1,0,0) rot=(0,1,0;1.5708rad)
  Radius = 11.1
FEATURE [Sketcher::SketchObject] Sketch016  label="T015"
  Placement = pos=(170.856,0,-10.6) rot=(1,0,0;1.5708rad)
  sketch-geometry (3):
    g0: LineSegment StartX=0.00120621 StartY=1.19996 StartZ=0 EndX=-0.691594 EndY=0 EndZ=0
    g1: LineSegment StartX=0.694006 StartY=0 StartZ=0 EndX=0.00120621 EndY=1.19996 EndZ=0
    g2: LineSegment StartX=-0.691594 StartY=0 StartZ=0 EndX=0.694006 EndY=0 EndZ=0
  constraints (8):
    c: PointOnObject(g1,g-1)
    c: Coincident(g1,g0)
    c: Coincident(g2,g0)
    c: Coincident(g2,g1)
    c: Horizontal(g2)
    c: Angle(g2,g0) = 1.0472
    c: Angle(g1,g2) = 1.0472
    c: Distance(g0,g0) = 1.3856
FEATURE [Part::Cylinder] Cylinder002  label="Cylinder"
  Angle = 360
  AttacherType = Attacher::AttachEngine3D
  Height = 197
  Placement = pos=(1,0,0) rot=(0,1,0;1.5708rad)
  Radius = 12.5
FEATURE [Part::Cut] Cut001
  Base = -> Cylinder002
  Tool = -> Cylinder003
FEATURE [Part::Cylinder] Cylinder013  label="Cylinder011"
  Angle = 360
  AttacherType = Attacher::AttachEngine3D
  Height = 2
  Placement = pos=(155.5,0,0) rot=(0,1,0;1.5708rad)
  Radius = 11.05
FEATURE [Part::Helix] Helix003
  Angle = 0
  AttacherType = Attacher::AttachEngine3D
  Height = 13.856
  LocalCoord = 0
  Pitch = 1.3856
  Placement = pos=(157,0,0) rot=(0,1,0;1.5708rad)
  Radius = 9.5
  Style = 1
FEATURE [Part::Sweep] Sweep004
  Frenet = true
  Sections = -> [Sketch007]
  Solid = true
  Spine = -> Helix003
  Transition = 1
FEATURE [Part::Cylinder] Cylinder015  label="Cylinder014"
  Angle = 360
  AttacherType = Attacher::AttachEngine3D
  Height = 25
  Placement = pos=(150,0,0) rot=(0,1,0;1.5708rad)
  Radius = 9.5
FEATURE [Part::Cut] Cut006
  Base = -> Sweep004
  Tool = -> Cylinder015
FEATURE [Part::Cylinder] Cylinder014  label="Cylinder013"
  Angle = 360
  AttacherType = Attacher::AttachEngine3D
  Height = 2
  Placement = pos=(155.5,0,0) rot=(0,1,0;1.5708rad)
  Radius = 9.5
FEATURE [Part::Cut] Cut004
  Base = -> Cylinder013
  Tool = -> Cylinder014
FEATURE [Part::MultiFuse] Fusion001
  Shapes = -> [Cut006,Cut004]
FEATURE [Part::Cut] Cut002  label="BatteryHolder"
  Base = -> Cut001
  Tool = -> Cylinder004
FEATURE [Part::Sweep] Sweep010
  Frenet = true
  Sections = -> [Sketch016]
  Solid = true
  Spine = -> Helix010
  Transition = 1
FEATURE [Part::Cut] Cut007
  Base = -> Sweep010
  Tool = -> Cylinder015
FEATURE [Part::MultiFuse] Fusion002
  Shapes = -> [Cut007,Fusion001]
FEATURE [Part::MultiFuse] Fusion003  label="BatHolderThread"
  Shapes = -> [Fusion002,Cut002]
FEATURE [Drawing::FeatureViewPart] Ortho020  label="Ortho_0_010"
  Direction = (1,0,0)
  HiddenWidth = 0.15
  LineWidth = 0.35
  Rotation = -90
  ShowHiddenLines = false
  ShowSmoothLines = false
  Source = -> Fusion003
  Tolerance = 0.05
  ViewResult = <blob: 9986 chars omitted>
  Visible = false
  X = 53.875
  Y = 81.5
FEATURE [Drawing::FeatureViewPart] Ortho021  label="Ortho_1_005"
  Direction = (0,1,0)
  HiddenWidth = 0.15
  LineWidth = 0.35
  Rotation = -90
  ShowHiddenLines = true
  ShowSmoothLines = false
  Source = -> Fusion003
  Tolerance = 0.05
  ViewResult = <blob: 47216 chars omitted>
  Visible = false
  X = 277.25
  Y = 81.5
FEATURE [Drawing::FeatureViewPart] Ortho022  label="Ortho_2_001"
  Direction = (-1,0,0)
  HiddenWidth = 0.15
  LineWidth = 0.35
  Rotation = 90
  ShowHiddenLines = false
  ShowSmoothLines = false
  Source = -> Fusion003
  Tolerance = 0.05
  ViewResult = <g id="Ortho_2_001"\n   transform="rotate(90,243.125,81.5) translate(243.125,81.5) scale(1,1)"\n  >\n<g   fill="none"\n   stroke="rgb(0, 0, 0)"\n   stroke-linecap="butt"\n   stroke-linejoin="miter"\n   stroke-width="0.350000"\n   transform="scale(1,-1)"\n  >\n<path d="M-9.95946,4.90093 Q-10.1632,4.43047 -10.3225,3.94322 " /><path d="M-11.1,0.00267469 C-11.101,1.69406 -10.7075,3.38396 -9.95946,4.90093 " /><path d="M-10.5097,-3.41317 C-10.8834,-2.31747 -11.0839,-1.16015 -11.1,0.00267469 " /><path d="M9.5,-0.0015244 L9.5,-0.00202623 " /><path d="M9.5,-0.00203307 Q9.49992,-0.363305 9.4724,-0.723571 " /><path d="M9.32043,-1.83836 Q9.17143,-2.59322 8.90311,-3.31431 " /><path d="M8.07486,-5.00466 Q7.90197,-5.2836 7.71028,-5.54992 " /><path d="M-10.5095,-3.41366 C-10.8841,-2.31545 -11.0839,-1.15796 -11.1,0.00228746 " /><circle cx ="0" cy ="0" r ="11.1" /><path d="M-11.1,0.00228746 L-11.1,0.00267469 " /><circle cx ="0" cy ="0" r ="12.5" /><path d="M-9.5,0.000122513 C-9.49995,0.0184956 -9.49989,0.0368686 -9.49984,0.0552417  C-9.49311,1.35202 -9.21629,2.64711 -8.69229,3.8333  C-8.16978,5.02015 -7.40017,6.09791 -6.44717,6.97739  C-4.92881,8.38709 -2.93717,9.27414 -0.873621,9.45975  C0.50771,9.58834 1.91655,9.40855 3.22132,8.93718  C5.25681,8.2097 7.02303,6.76093 8.13456,4.90703  C9.02472,3.43599 9.50238,1.7194 9.5,-4.04121e-14 " /><circle cx ="0" cy ="0" r ="11.05" /><circle cx ="0" cy ="0" r ="9.5" /></g>\n</g>
  Visible = false
  X = 243.125
  Y = 81.5
FEATURE [Drawing::FeatureViewPython] dia027  # drawing view (typed FeaturePython)
  Rotation = 0
  ViewResult = <g>  <circle cx ="53.873613" cy ="81.495730" r="0.250000" stroke="none" fill="rgb(255,0,0)" /> \n<line x1="33.487025" y1="52.731467" x2="59.369479" y2="89.250069" style="stroke:rgb(255,0,0);stroke-width:0.10" />\n<polygon points="48.377748,73.741390 49.126299,75.662242 49.823353,75.781053 49.942164,75.084000" style="fill:rgb(255,0,0);stroke:rgb(255,0,0);stroke-width:0" />\n<polygon points="59.369479,89.250069 58.620928,87.329218 57.923874,87.210406 57.805062,87.907460" style="fill:rgb(255,0,0);stroke:rgb(255,0,0);stroke-width:0" />\n<line x1="33.487025" y1="52.731467" x2="16.785901" y2="52.731467" style="stroke:rgb(255,0,0);stroke-width:0.10" />\n<text x="25.136463" y="50.731467" font-family="inherit" font-size="3.6" fill="rgb(0,0,0)" text-anchor="middle" transform="rotate(0.000000 25.136463,50.731467)" >Ø19</text> </g>
  Visible = false
  X = 0
  Y = 0
  arrowL1 = 2
  arrowL2 = 0.5
  arrowW = 1
  arrow_scheme = 0
  autoPlaceOffset = 2
  autoPlaceText = true
  centerPointDia = 0.5
  click1_x = 33.487
  click1_y = 52.7315
  click2_x = 16.7859
  click2_y = 52.6467
  click3_x = 16.7859
  click3_y = 52.6467
  comma_decimal_place = false
  lineColor = rgb(255,0,0)
  strokeWidth = 0.1
  textFormat_circular = Ø%(value)3.1f
  textRenderer_color = rgb(0,0,0)
  textRenderer_family = inherit
  textRenderer_size = 3.6
  unit_custom_scale = 1.7
  unit_scheme = 0
FEATURE [Drawing::FeatureViewPython] dim158  # drawing view (typed FeaturePython)
  Rotation = 0
  ViewResult = <g> \n  <line x1="121.750000" y1="72.000000" x2="140.293323" y2="72.000000" style="stroke:rgb(255,0,0);stroke-width:0.10" />\n<line x1="121.750000" y1="91.000000" x2="140.293323" y2="91.000000" style="stroke:rgb(255,0,0);stroke-width:0.10" />\n<line x1="139.293323" y1="72.000000" x2="139.293323" y2="91.000000" style="stroke:rgb(255,0,0);stroke-width:0.10" /> \n  <polygon points="139.293323,91.000000 139.793323,89.000000 139.293323,88.500000 138.793323,89.000000" style="fill:rgb(255,0,0);stroke:rgb(255,0,0);stroke-width:0" /><polygon points="139.293323,72.000000 138.793323,74.000000 139.293323,74.500000 139.793323,74.000000" style="fill:rgb(255,0,0);stroke:rgb(255,0,0);stroke-width:0" /> \n  <text x="137.293323" y="81.500000" font-family="inherit" font-size="3.6" fill="rgb(0,0,0)" text-anchor="middle" transform="rotate(-90.000000 137.293323,81.500000)" >19</text> </g>
  Visible = false
  X = 0
  Y = 0
  arrowL1 = 2
  arrowL2 = 0.5
  arrowW = 1
  arrow_scheme = 0
  autoPlaceOffset = 2
  autoPlaceText = true
  click1_x = 139.293
  click1_y = 89.9108
  click2_x = 139.293
  click2_y = 89.9108
  comma_decimal_place = false
  dimension_line_overshoot = 1
  gap_datum_points = 0
  halfDimension_linear = false
  lineColor = rgb(255,0,0)
  strokeWidth = 0.1
  textFormat_linear = %(value)3.3f
  textRenderer_color = rgb(0,0,0)
  textRenderer_family = inherit
  textRenderer_size = 3.6
  unit_custom_scale = 1.7
  unit_scheme = 0
FEATURE [Drawing::FeatureViewPython] dim159  # drawing view (typed FeaturePython)
  Rotation = 0
  ViewResult = <g> \n  <line x1="121.750000" y1="70.450000" x2="152.578433" y2="70.450000" style="stroke:rgb(255,0,0);stroke-width:0.10" />\n<line x1="121.750000" y1="92.550000" x2="152.578433" y2="92.550000" style="stroke:rgb(255,0,0);stroke-width:0.10" />\n<line x1="151.578433" y1="70.450000" x2="151.578433" y2="92.550000" style="stroke:rgb(255,0,0);stroke-width:0.10" /> \n  <polygon points="151.578433,92.550000 152.078433,90.550000 151.578433,90.050000 151.078433,90.550000" style="fill:rgb(255,0,0);stroke:rgb(255,0,0);stroke-width:0" /><polygon points="151.578433,70.450000 151.078433,72.450000 151.578433,72.950000 152.078433,72.450000" style="fill:rgb(255,0,0);stroke:rgb(255,0,0);stroke-width:0" /> \n  <text x="149.578433" y="81.500000" font-family="inherit" font-size="3.6" fill="rgb(0,0,0)" text-anchor="middle" transform="rotate(-90.000000 149.578433,81.500000)" >22.1</text> </g>
  Visible = false
  X = 0
  Y = 0
  arrowL1 = 2
  arrowL2 = 0.5
  arrowW = 1
  arrow_scheme = 0
  autoPlaceOffset = 2
  autoPlaceText = true
  click1_x = 151.578
  click1_y = 92.6519
  click2_x = 151.578
  click2_y = 92.6519
  comma_decimal_place = false
  dimension_line_overshoot = 1
  gap_datum_points = 0
  halfDimension_linear = false
  lineColor = rgb(255,0,0)
  strokeWidth = 0.1
  textFormat_linear = %(value)3.3f
  textRenderer_color = rgb(0,0,0)
  textRenderer_family = inherit
  textRenderer_size = 3.6
  unit_custom_scale = 1.7
  unit_scheme = 0
FEATURE [Drawing::FeatureViewPython] dia022  # drawing view (typed FeaturePython)
  Rotation = 0
  ViewResult = <g>  <circle cx ="243.125000" cy ="81.500000" r="0.250000" stroke="none" fill="rgb(255,0,0)" /> \n<line x1="255.744788" y1="112.753780" x2="239.568069" y2="72.691014" style="stroke:rgb(255,0,0);stroke-width:0.10" />\n<polygon points="246.681931,90.308986 246.396734,88.267256 245.745897,87.990832 245.469473,88.641670" style="fill:rgb(255,0,0);stroke:rgb(255,0,0);stroke-width:0" />\n<polygon points="239.568069,72.691014 239.853266,74.732744 240.504103,75.009168 240.780527,74.358330" style="fill:rgb(255,0,0);stroke:rgb(255,0,0);stroke-width:0" />\n<line x1="255.744788" y1="112.753780" x2="268.461380" y2="112.753780" style="stroke:rgb(255,0,0);stroke-width:0.10" />\n<text x="262.103084" y="110.753780" font-family="inherit" font-size="3.6" fill="rgb(0,0,0)" text-anchor="middle" transform="rotate(0.000000 262.103084,110.753780)" >Ø19</text> </g>
  Visible = false
  X = 0
  Y = 0
  arrowL1 = 2
  arrowL2 = 0.5
  arrowW = 1
  arrow_scheme = 0
  autoPlaceOffset = 2
  autoPlaceText = true
  centerPointDia = 0.5
  click1_x = 255.745
  click1_y = 112.754
  click2_x = 268.461
  click2_y = 113.46
  click3_x = 268.461
  click3_y = 113.46
  comma_decimal_place = false
  lineColor = rgb(255,0,0)
  strokeWidth = 0.1
  textFormat_circular = Ø%(value)3.3f
  textRenderer_color = rgb(0,0,0)
  textRenderer_family = inherit
  textRenderer_size = 3.6
  unit_custom_scale = 1.7
  unit_scheme = 0
FEATURE [Drawing::FeatureViewPython] dia023  # drawing view (typed FeaturePython)
  Rotation = 0
  ViewResult = <g>  <circle cx ="243.125000" cy ="81.500000" r="0.250000" stroke="none" fill="rgb(255,0,0)" /> \n<line x1="260.195596" y1="61.816765" x2="236.900705" y2="88.676918" style="stroke:rgb(255,0,0);stroke-width:0.10" />\n<polygon points="249.349295,74.323082 247.661185,75.506418 247.711323,76.211745 248.416650,76.161607" style="fill:rgb(255,0,0);stroke:rgb(255,0,0);stroke-width:0" />\n<polygon points="236.900705,88.676918 238.588815,87.493582 238.538677,86.788255 237.833350,86.838393" style="fill:rgb(255,0,0);stroke:rgb(255,0,0);stroke-width:0" />\n<line x1="260.195596" y1="61.816765" x2="271.287289" y2="61.816765" style="stroke:rgb(255,0,0);stroke-width:0.10" />\n<text x="265.741443" y="59.816765" font-family="inherit" font-size="3.6" fill="rgb(0,0,0)" text-anchor="middle" transform="rotate(0.000000 265.741443,59.816765)" >Ø19</text> </g>
  Visible = false
  X = 0
  Y = 0
  arrowL1 = 2
  arrowL2 = 0.5
  arrowW = 1
  arrow_scheme = 0
  autoPlaceOffset = 2
  autoPlaceText = true
  centerPointDia = 0.5
  click1_x = 260.196
  click1_y = 61.8168
  click2_x = 271.287
  click2_y = 61.8168
  click3_x = 271.287
  click3_y = 61.8168
  comma_decimal_place = false
  lineColor = rgb(255,0,0)
  strokeWidth = 0.1
  textFormat_circular = Ø%(value)3.3f
  textRenderer_color = rgb(0,0,0)
  textRenderer_family = inherit
  textRenderer_size = 3.6
  unit_custom_scale = 1.7
  unit_scheme = 0
FEATURE [Drawing::FeaturePage] Page009  label="BatteryHolder2-SV"
  EditableTexts = Dr. Zoidberg | 05.02.2019 | x1.0 | unknown | ERG-T-01 | Battery Holder. Side view. | 04 | 04
  Group = -> [Ortho022,Ortho021,Ortho020,dia024,dia025,dim145,dim147,dim148,dim149,dim150,dim151,dim155,dim152,dim153,dim154,dim156,dim157,dia026,dia027,dim158,dim159,dia022,dia023]
  Template = <path>//share/freecad/Mod/Drawing/Templates/A4_Landscape.svg
FEATURE [Part::Cylinder] Cylinder016  label="Cylinder018"
  Angle = 360
  AttacherType = Attacher::AttachEngine3D
  Height = 27.1
  Placement = pos=(172.9,0,0) rot=(0,1,0;1.5708rad)
  Radius = 10.7
FEATURE [Part::Cylinder] Cylinder017  label="Cylinder019"
  Angle = 360
  AttacherType = Attacher::AttachEngine3D
  Height = 170
  Placement = pos=(1,0,0) rot=(0,1,0;1.5708rad)
  Radius = 11.1
FEATURE [Part::Cylinder] Cylinder018  label="Cylinder020"
  Angle = 360
  AttacherType = Attacher::AttachEngine3D
  Height = 199
  Placement = pos=(1,0,0) rot=(0,1,0;1.5708rad)
  Radius = 12.5
FEATURE [Part::Cylinder] Cylinder019  label="Cylinder021"
  Angle = 360
  AttacherType = Attacher::AttachEngine3D
  Height = 1.9
  Placement = pos=(171,0,0) rot=(0,1,0;1.5708rad)
  Radius = 9.5
FEATURE [Part::MultiFuse] Fusion
  Shapes = -> [Cylinder016,Cylinder017,Cylinder019]
FEATURE [Part::Cut] Cut
  Base = -> Cylinder018
  Tool = -> Fusion
FEATURE [Sketcher::SketchObject] Sketch017  label="T016"
  Placement = pos=(157,0,-10.8) rot=(1,0,0;1.5708rad)
  sketch-geometry (3):
    g0: LineSegment StartX=0.00120621 StartY=1.19996 StartZ=0 EndX=-0.691594 EndY=0 EndZ=0
    g1: LineSegment StartX=0.694006 StartY=0 StartZ=0 EndX=0.00120621 EndY=1.19996 EndZ=0
    g2: LineSegment StartX=-0.691594 StartY=0 StartZ=0 EndX=0.694006 EndY=0 EndZ=0
  constraints (8):
    c: PointOnObject(g1,g-1)
    c: Coincident(g1,g0)
    c: Coincident(g2,g0)
    c: Coincident(g2,g1)
    c: Horizontal(g2)
    c: Angle(g2,g0) = 1.0472
    c: Angle(g1,g2) = 1.0472
    c: Distance(g0,g0) = 1.3856
FEATURE [Part::Cylinder] Cylinder020  label="Cylinder022"
  Angle = 360
  AttacherType = Attacher::AttachEngine3D
  Height = 2
  Placement = pos=(155.5,0,0) rot=(0,1,0;1.5708rad)
  Radius = 11.05
FEATURE [Part::Helix] Helix011
  Angle = 0
  AttacherType = Attacher::AttachEngine3D
  Height = 16.64
  LocalCoord = 0
  Pitch = 1.3856
  Placement = pos=(157,0,0) rot=(0,1,0;1.5708rad)
  Radius = 9.5
  Style = 1
FEATURE [Part::Sweep] Sweep011
  Frenet = true
  Sections = -> [Sketch017]
  Solid = true
  Spine = -> Helix011
  Transition = 1
FEATURE [Part::Cylinder] Cylinder021  label="Cylinder023"
  Angle = 360
  AttacherType = Attacher::AttachEngine3D
  Height = 25
  Placement = pos=(150,0,0) rot=(0,1,0;1.5708rad)
  Radius = 9.7
FEATURE [Part::Cut] Cut009
  Base = -> Sweep011
  Tool = -> Cylinder021
FEATURE [Part::Cylinder] Cylinder022  label="Cylinder024"
  Angle = 360
  AttacherType = Attacher::AttachEngine3D
  Height = 2
  Placement = pos=(155.5,0,0) rot=(0,1,0;1.5708rad)
  Radius = 9.5
FEATURE [Part::Cut] Cut008
  Base = -> Cylinder020
  Tool = -> Cylinder022
FEATURE [Part::MultiFuse] Fusion004
  Placement = pos=(15.5,0,0) rot=(0,0,1;0rad)
  Shapes = -> [Cut009,Cut008]
FEATURE [Part::Cylinder] Cylinder023  label="Cylinder025"
  Angle = 360
  AttacherType = Attacher::AttachEngine3D
  Height = 12.5
  Placement = pos=(187.5,0,0) rot=(0,1,0;1.5708rad)
  Radius = 11
FEATURE [Part::Cut] Cut010
  Base = -> Fusion004
  Tool = -> Cylinder023
FEATURE [Part::MultiFuse] Fusion005
  Shapes = -> [Cut010,Cut]
FEATURE [Part::Helix] Helix012
  Angle = 0
  AttacherType = Attacher::AttachEngine3D
  Height = 16.64
  LocalCoord = 0
  Pitch = 0.578
  Placement = pos=(157,0,0) rot=(0,1,0;1.5708rad)
  Radius = 9.5
  Style = 1
FEATURE [Sketcher::SketchObject] Sketch018  label="T017"
  Placement = pos=(156.5,0,-11.55) rot=(1,0,0;1.5708rad)
  sketch-geometry (3):
    g0: LineSegment StartX=0.0792305 StartY=0.500193 StartZ=0 EndX=0.65623 EndY=0.500193 EndZ=0
    g1: LineSegment StartX=0.0792305 StartY=0.500193 StartZ=0 EndX=0.36773 EndY=0.000495962 EndZ=0
    g2: LineSegment StartX=0.36773 StartY=0.000495962 StartZ=0 EndX=0.65623 EndY=0.500193 EndZ=0
  constraints (7):
    c: Horizontal(g0)
    c: DistanceX(g0,g0) = 0.577
    c: Coincident(g1,g0)
    c: Coincident(g2,g1)
    c: Coincident(g2,g0)
    c: Angle(g1,g0) = 1.0472
    c: Angle(g0,g2) = 1.0472
FEATURE [Part::Sweep] Sweep012
  Frenet = true
  Placement = pos=(-156.5,0,0) rot=(0,0,1;0rad)
  Sections = -> [Sketch018]
  Solid = true
  Spine = -> Helix012
  Transition = 1
FEATURE [Part::Cylinder] Cylinder  label="Cylinder029"
  Angle = 360
  AttacherType = Attacher::AttachEngine3D
  Height = 3
  Placement = pos=(16,0,0) rot=(0,1,0;1.5708rad)
  Radius = 13
FEATURE [Part::Cylinder] Cylinder027  label="Cylinder030"
  Angle = 360
  AttacherType = Attacher::AttachEngine3D
  Height = 3
  Placement = pos=(-2,0,0) rot=(0,1,0;1.5708rad)
  Radius = 13
FEATURE [Part::MultiFuse] Fusion006
  Shapes = -> [Cylinder,Cylinder027]
FEATURE [Part::Cylinder] Cylinder028  label="Cylinder031"
  Angle = 360
  AttacherType = Attacher::AttachEngine3D
  Height = 15
  Placement = pos=(1,0,0) rot=(0,1,0;1.5708rad)
  Radius = 13
FEATURE [Part::Cylinder] Cylinder029  label="Cylinder032"
  Angle = 360
  AttacherType = Attacher::AttachEngine3D
  Height = 15
  Placement = pos=(1,0,0) rot=(0,1,0;1.5708rad)
  Radius = 11.5
FEATURE [Part::Cut] Cut014
  Base = -> Cylinder028
  Tool = -> Cylinder029
FEATURE [Part::MultiFuse] Fusion007
  Shapes = -> [Fusion006,Cut014]
FEATURE [Part::Cut] Cut015
  Base = -> Sweep012
  Tool = -> Fusion007
FEATURE [Part::Cut] Cut016  label="BatteryHolder3"
  Base = -> Fusion005
  Tool = -> Cut015
FEATURE [Drawing::FeatureViewPart] Ortho  label="Ortho_0_0"
  Direction = (1,0,0)
  HiddenWidth = 0.15
  LineWidth = 0.35
  Rotation = -90
  Scale = 0.75
  ShowHiddenLines = false
  ShowSmoothLines = false
  Source = -> Cut016
  Tolerance = 0.05
  ViewResult = <blob: 2041 chars omitted>
  Visible = false
  X = 41.9375
  Y = 81.5
FEATURE [Drawing::FeatureViewPart] Ortho023  label="Ortho_1_0"
  Direction = (0,1,0)
  HiddenWidth = 0.15
  LineWidth = 0.35
  Rotation = -90
  Scale = 0.75
  ShowHiddenLines = true
  ShowSmoothLines = false
  Source = -> Cut016
  Tolerance = 0.05
  ViewResult = <blob: 139204 chars omitted>
  Visible = false
  X = 223.875
  Y = 81.5
FEATURE [Drawing::FeatureViewPart] Ortho024  label="Ortho_2_0"
  Direction = (-1,0,0)
  HiddenWidth = 0.15
  LineWidth = 0.35
  Rotation = 90
  Scale = 0.75
  ShowHiddenLines = false
  ShowSmoothLines = false
  Source = -> Cut016
  Tolerance = 0.05
  ViewResult = <blob: 24610 chars omitted>
  Visible = false
  X = 255.062
  Y = 81.5
FEATURE [Part::Feature] Cut016_cs
  shape: bbox 199 x 25 x 1e-05 mm, 0 faces, 0 solids (baked)
FEATURE [Drawing::FeatureViewPart] Ortho025  label="Ortho_0_011"
  Direction = (0,0,1)
  HiddenWidth = 0.15
  LineWidth = 0.15
  Rotation = 180
  ShowHiddenLines = false
  ShowSmoothLines = false
  Source = -> Cut016_cs
  Tolerance = 0.05
  ViewResult = <blob: 15736 chars omitted>
  Visible = false
  X = 249
  Y = 81.5
FEATURE [Drawing::FeatureViewPython] dim002  # drawing view (typed FeaturePython)
  Rotation = 0
  ViewResult = <g> \n  <line x1="49.000000" y1="69.000000" x2="27.763548" y2="69.000000" style="stroke:rgb(255,0,0);stroke-width:0.10" />\n<line x1="49.000000" y1="94.000000" x2="27.763548" y2="94.000000" style="stroke:rgb(255,0,0);stroke-width:0.10" />\n<line x1="28.763548" y1="69.000000" x2="28.763548" y2="94.000000" style="stroke:rgb(255,0,0);stroke-width:0.10" /> \n  <polygon points="28.763548,94.000000 29.263548,92.000000 28.763548,91.500000 28.263548,92.000000" style="fill:rgb(255,0,0);stroke:rgb(255,0,0);stroke-width:0" /><polygon points="28.763548,69.000000 28.263548,71.000000 28.763548,71.500000 29.263548,71.000000" style="fill:rgb(255,0,0);stroke:rgb(255,0,0);stroke-width:0" /> \n  <text x="26.763548" y="81.500000" font-family="inherit" font-size="3.6" fill="rgb(0,0,0)" text-anchor="middle" transform="rotate(-90.000000 26.763548,81.500000)" >25</text> </g>
  Visible = false
  X = 0
  Y = 0
  arrowL1 = 2
  arrowL2 = 0.5
  arrowW = 1
  arrow_scheme = 0
  autoPlaceOffset = 2
  autoPlaceText = true
  click1_x = 28.7635
  click1_y = 94.0942
  click2_x = 28.7635
  click2_y = 94.0942
  comma_decimal_place = false
  dimension_line_overshoot = 1
  gap_datum_points = 0
  halfDimension_linear = false
  lineColor = rgb(255,0,0)
  strokeWidth = 0.1
  textFormat_linear = %(value)3.3f
  textRenderer_color = rgb(0,0,0)
  textRenderer_family = inherit
  textRenderer_size = 3.6
  unit_custom_scale = 1
  unit_scheme = 0
FEATURE [Drawing::FeatureViewPython] dim003  # drawing view (typed FeaturePython)
  Rotation = 0
  ViewResult = <g> \n  <line x1="49.000000" y1="70.800000" x2="36.147542" y2="70.800000" style="stroke:rgb(255,0,0);stroke-width:0.10" />\n<line x1="49.000000" y1="92.200000" x2="36.147542" y2="92.200000" style="stroke:rgb(255,0,0);stroke-width:0.10" />\n<line x1="37.147542" y1="70.800000" x2="37.147542" y2="92.200000" style="stroke:rgb(255,0,0);stroke-width:0.10" /> \n  <polygon points="37.147542,92.200000 37.647542,90.200000 37.147542,89.700000 36.647542,90.200000" style="fill:rgb(255,0,0);stroke:rgb(255,0,0);stroke-width:0" /><polygon points="37.147542,70.800000 36.647542,72.800000 37.147542,73.300000 37.647542,72.800000" style="fill:rgb(255,0,0);stroke:rgb(255,0,0);stroke-width:0" /> \n  <text x="35.147542" y="81.500000" font-family="inherit" font-size="3.6" fill="rgb(0,0,0)" text-anchor="middle" transform="rotate(-90.000000 35.147542,81.500000)" >21.4</text> </g>
  Visible = false
  X = 0
  Y = 0
  arrowL1 = 2
  arrowL2 = 0.5
  arrowW = 1
  arrow_scheme = 0
  autoPlaceOffset = 2
  autoPlaceText = true
  click1_x = 37.1475
  click1_y = 90.5471
  click2_x = 37.1475
  click2_y = 90.5471
  comma_decimal_place = false
  dimension_line_overshoot = 1
  gap_datum_points = 0
  halfDimension_linear = false
  lineColor = rgb(255,0,0)
  strokeWidth = 0.1
  textFormat_linear = %(value)3.3f
  textRenderer_color = rgb(0,0,0)
  textRenderer_family = inherit
  textRenderer_size = 3.6
  unit_custom_scale = 1
  unit_scheme = 0
FEATURE [Drawing::FeatureViewPython] dim004  # drawing view (typed FeaturePython)
  Rotation = 0
  ViewResult = <g> \n  <line x1="61.661000" y1="71.800000" x2="43.886613" y2="71.800000" style="stroke:rgb(255,0,0);stroke-width:0.10" />\n<line x1="62.354000" y1="91.200000" x2="43.886613" y2="91.200000" style="stroke:rgb(255,0,0);stroke-width:0.10" />\n<line x1="44.886613" y1="71.800000" x2="44.886613" y2="91.200000" style="stroke:rgb(255,0,0);stroke-width:0.10" /> \n  <polygon points="44.886613,91.200000 45.386613,89.200000 44.886613,88.700000 44.386613,89.200000" style="fill:rgb(255,0,0);stroke:rgb(255,0,0);stroke-width:0" /><polygon points="44.886613,71.800000 44.386613,73.800000 44.886613,74.300000 45.386613,73.800000" style="fill:rgb(255,0,0);stroke:rgb(255,0,0);stroke-width:0" /> \n  <text x="42.886613" y="81.500000" font-family="inherit" font-size="3.6" fill="rgb(0,0,0)" text-anchor="middle" transform="rotate(-90.000000 42.886613,81.500000)" >19.4</text> </g>
  Visible = false
  X = 0
  Y = 0
  arrowL1 = 2
  arrowL2 = 0.5
  arrowW = 1
  arrow_scheme = 0
  autoPlaceOffset = 2
  autoPlaceText = true
  click1_x = 44.8866
  click1_y = 89.4637
  click2_x = 44.8866
  click2_y = 89.4637
  comma_decimal_place = false
  dimension_line_overshoot = 1
  gap_datum_points = 0
  halfDimension_linear = false
  lineColor = rgb(255,0,0)
  strokeWidth = 0.1
  textFormat_linear = %(value)3.3f
  textRenderer_color = rgb(0,0,0)
  textRenderer_family = inherit
  textRenderer_size = 3.6
  unit_custom_scale = 1
  unit_scheme = 0
FEATURE [Drawing::FeatureViewPython] dim005  # drawing view (typed FeaturePython)
  Rotation = 0
  ViewResult = <g> \n  <line x1="78.000000" y1="72.000000" x2="78.000000" y2="61.609086" style="stroke:rgb(255,0,0);stroke-width:0.10" />\n<line x1="76.100000" y1="72.000000" x2="76.100000" y2="61.609086" style="stroke:rgb(255,0,0);stroke-width:0.10" />\n<line x1="78.000000" y1="62.609086" x2="76.100000" y2="62.609086" style="stroke:rgb(255,0,0);stroke-width:0.10" /> \n  <polygon points="76.100000,62.609086 74.100000,62.109086 73.600000,62.609086 74.100000,63.109086" style="fill:rgb(255,0,0);stroke:rgb(255,0,0);stroke-width:0" /><polygon points="78.000000,62.609086 80.000000,63.109086 80.500000,62.609086 80.000000,62.109086" style="fill:rgb(255,0,0);stroke:rgb(255,0,0);stroke-width:0" /> \n  <text x="77.050000" y="60.609086" font-family="inherit" font-size="3.6" fill="rgb(0,0,0)" text-anchor="middle" transform="rotate(0.000000 77.050000,60.609086)" >1.9</text> </g>
  Visible = false
  X = 0
  Y = 0
  arrowL1 = 2
  arrowL2 = 0.5
  arrowW = 1
  arrow_scheme = 0
  autoPlaceOffset = 2
  autoPlaceText = true
  click1_x = 76.7716
  click1_y = 62.6091
  click2_x = 76.7716
  click2_y = 62.6091
  comma_decimal_place = false
  dimension_line_overshoot = 1
  gap_datum_points = 0
  halfDimension_linear = false
  lineColor = rgb(255,0,0)
  strokeWidth = 0.1
  textFormat_linear = %(value)3.3f
  textRenderer_color = rgb(0,0,0)
  textRenderer_family = inherit
  textRenderer_size = 3.6
  unit_custom_scale = 1
  unit_scheme = 0
FEATURE [Drawing::FeatureViewPython] dim006  # drawing view (typed FeaturePython)
  Rotation = 0
  ViewResult = <g> \n  <line x1="76.100000" y1="72.000000" x2="76.100000" y2="61.620819" style="stroke:rgb(255,0,0);stroke-width:0.10" />\n<line x1="61.500000" y1="70.800000" x2="61.500000" y2="61.620819" style="stroke:rgb(255,0,0);stroke-width:0.10" />\n<line x1="76.100000" y1="62.620819" x2="61.500000" y2="62.620819" style="stroke:rgb(255,0,0);stroke-width:0.10" /> \n  <polygon points="61.500000,62.620819 63.500000,63.120819 64.000000,62.620819 63.500000,62.120819" style="fill:rgb(255,0,0);stroke:rgb(255,0,0);stroke-width:0" /><polygon points="76.100000,62.620819 74.100000,62.120819 73.600000,62.620819 74.100000,63.120819" style="fill:rgb(255,0,0);stroke:rgb(255,0,0);stroke-width:0" /> \n  <text x="68.800000" y="60.620819" font-family="inherit" font-size="3.6" fill="rgb(0,0,0)" text-anchor="middle" transform="rotate(0.000000 68.800000,60.620819)" >14.6</text> </g>
  Visible = false
  X = 0
  Y = 0
  arrowL1 = 2
  arrowL2 = 0.5
  arrowW = 1
  arrow_scheme = 0
  autoPlaceOffset = 2
  autoPlaceText = true
  click1_x = 63.9836
  click1_y = 62.6208
  click2_x = 63.9836
  click2_y = 62.6208
  comma_decimal_place = false
  dimension_line_overshoot = 1
  gap_datum_points = 0
  halfDimension_linear = false
  lineColor = rgb(255,0,0)
  strokeWidth = 0.1
  textFormat_linear = %(value)3.3f
  textRenderer_color = rgb(0,0,0)
  textRenderer_family = inherit
  textRenderer_size = 3.6
  unit_custom_scale = 1
  unit_scheme = 0
FEATURE [Drawing::FeatureViewPython] dim007  # drawing view (typed FeaturePython)
  Rotation = 0
  ViewResult = <g> \n  <line x1="61.500000" y1="70.800000" x2="61.500000" y2="61.654889" style="stroke:rgb(255,0,0);stroke-width:0.10" />\n<line x1="49.000000" y1="70.800000" x2="49.000000" y2="61.654889" style="stroke:rgb(255,0,0);stroke-width:0.10" />\n<line x1="61.500000" y1="62.654889" x2="49.000000" y2="62.654889" style="stroke:rgb(255,0,0);stroke-width:0.10" /> \n  <polygon points="49.000000,62.654889 51.000000,63.154889 51.500000,62.654889 51.000000,62.154889" style="fill:rgb(255,0,0);stroke:rgb(255,0,0);stroke-width:0" /><polygon points="61.500000,62.654889 59.500000,62.154889 59.000000,62.654889 59.500000,63.154889" style="fill:rgb(255,0,0);stroke:rgb(255,0,0);stroke-width:0" /> \n  <text x="55.250000" y="60.654889" font-family="inherit" font-size="3.6" fill="rgb(0,0,0)" text-anchor="middle" transform="rotate(0.000000 55.250000,60.654889)" >12.5</text> </g>
  Visible = false
  X = 0
  Y = 0
  arrowL1 = 2
  arrowL2 = 0.5
  arrowW = 1
  arrow_scheme = 0
  autoPlaceOffset = 2
  autoPlaceText = true
  click1_x = 60.3381
  click1_y = 62.6549
  click2_x = 60.3381
  click2_y = 62.6549
  comma_decimal_place = false
  dimension_line_overshoot = 1
  gap_datum_points = 0
  halfDimension_linear = false
  lineColor = rgb(255,0,0)
  strokeWidth = 0.1
  textFormat_linear = %(value)3.3f
  textRenderer_color = rgb(0,0,0)
  textRenderer_family = inherit
  textRenderer_size = 3.6
  unit_custom_scale = 1
  unit_scheme = 0
FEATURE [Drawing::FeatureViewPython] dim008  # drawing view (typed FeaturePython)
  Rotation = 0
  ViewResult = <g> \n  <line x1="49.000000" y1="94.000000" x2="49.000000" y2="103.620085" style="stroke:rgb(255,0,0);stroke-width:0.10" />\n<line x1="78.000000" y1="92.550000" x2="78.000000" y2="103.620085" style="stroke:rgb(255,0,0);stroke-width:0.10" />\n<line x1="49.000000" y1="102.620085" x2="78.000000" y2="102.620085" style="stroke:rgb(255,0,0);stroke-width:0.10" /> \n  <polygon points="78.000000,102.620085 76.000000,102.120085 75.500000,102.620085 76.000000,103.120085" style="fill:rgb(255,0,0);stroke:rgb(255,0,0);stroke-width:0" /><polygon points="49.000000,102.620085 51.000000,103.120085 51.500000,102.620085 51.000000,102.120085" style="fill:rgb(255,0,0);stroke:rgb(255,0,0);stroke-width:0" /> \n  <text x="63.500000" y="100.620085" font-family="inherit" font-size="3.6" fill="rgb(0,0,0)" text-anchor="middle" transform="rotate(0.000000 63.500000,100.620085)" >29</text> </g>
  Visible = false
  X = 0
  Y = 0
  arrowL1 = 2
  arrowL2 = 0.5
  arrowW = 1
  arrow_scheme = 0
  autoPlaceOffset = 2
  autoPlaceText = true
  click1_x = 75.7655
  click1_y = 102.62
  click2_x = 75.7655
  click2_y = 102.62
  comma_decimal_place = false
  dimension_line_overshoot = 1
  gap_datum_points = 0
  halfDimension_linear = false
  lineColor = rgb(255,0,0)
  strokeWidth = 0.1
  textFormat_linear = %(value)3.3f
  textRenderer_color = rgb(0,0,0)
  textRenderer_family = inherit
  textRenderer_size = 3.6
  unit_custom_scale = 1
  unit_scheme = 0
FEATURE [Drawing::FeatureViewPython] dim009  # drawing view (typed FeaturePython)
  Rotation = 0
  ViewResult = <g> \n  <line x1="78.000000" y1="92.550000" x2="77.978900" y2="103.647736" style="stroke:rgb(255,0,0);stroke-width:0.10" />\n<line x1="233.000000" y1="92.844700" x2="232.978900" y2="103.942436" style="stroke:rgb(255,0,0);stroke-width:0.10" />\n<line x1="77.980801" y1="102.647738" x2="232.980801" y2="102.942438" style="stroke:rgb(255,0,0);stroke-width:0.10" /> \n  <polygon points="232.980801,102.942438 230.981756,102.438636 230.480806,102.937685 230.979854,103.438634" style="fill:rgb(255,0,0);stroke:rgb(255,0,0);stroke-width:0" /><polygon points="77.980801,102.647738 79.979847,103.151539 80.480797,102.652491 79.981748,102.151541" style="fill:rgb(255,0,0);stroke:rgb(255,0,0);stroke-width:0" /> \n  <text x="155.484604" y="100.795091" font-family="inherit" font-size="3.6" fill="rgb(0,0,0)" text-anchor="middle" transform="rotate(0.108936 155.484604,100.795091)" >155</text> </g>
  Visible = false
  X = 0
  Y = 0
  arrowL1 = 2
  arrowL2 = 0.5
  arrowW = 1
  arrow_scheme = 0
  autoPlaceOffset = 2
  autoPlaceText = true
  click1_x = 76.0268
  click1_y = 102.644
  click2_x = 76.0268
  click2_y = 102.644
  comma_decimal_place = false
  dimension_line_overshoot = 1
  gap_datum_points = 0
  halfDimension_linear = false
  lineColor = rgb(255,0,0)
  strokeWidth = 0.1
  textFormat_linear = %(value)3.3f
  textRenderer_color = rgb(0,0,0)
  textRenderer_family = inherit
  textRenderer_size = 3.6
  unit_custom_scale = 1
  unit_scheme = 0
FEATURE [Drawing::FeatureViewPython] dim010  # drawing view (typed FeaturePython)
  Rotation = 0
  ViewResult = <g> \n  <line x1="78.000000" y1="70.400000" x2="97.362186" y2="70.400000" style="stroke:rgb(255,0,0);stroke-width:0.10" />\n<line x1="78.000000" y1="92.550000" x2="97.362186" y2="92.550000" style="stroke:rgb(255,0,0);stroke-width:0.10" />\n<line x1="96.362186" y1="70.400000" x2="96.362186" y2="92.550000" style="stroke:rgb(255,0,0);stroke-width:0.10" /> \n  <polygon points="96.362186,92.550000 96.862186,90.550000 96.362186,90.050000 95.862186,90.550000" style="fill:rgb(255,0,0);stroke:rgb(255,0,0);stroke-width:0" /><polygon points="96.362186,70.400000 95.862186,72.400000 96.362186,72.900000 96.862186,72.400000" style="fill:rgb(255,0,0);stroke:rgb(255,0,0);stroke-width:0" /> \n  <text x="94.362186" y="81.475000" font-family="inherit" font-size="3.6" fill="rgb(0,0,0)" text-anchor="middle" transform="rotate(-90.000000 94.362186,81.475000)" >22.2</text> </g>
  Visible = false
  X = 0
  Y = 0
  arrowL1 = 2
  arrowL2 = 0.5
  arrowW = 1
  arrow_scheme = 0
  autoPlaceOffset = 2
  autoPlaceText = true
  click1_x = 96.3622
  click1_y = 90.2892
  click2_x = 96.3622
  click2_y = 90.2892
  comma_decimal_place = false
  dimension_line_overshoot = 1
  gap_datum_points = 0
  halfDimension_linear = false
  lineColor = rgb(255,0,0)
  strokeWidth = 0.1
  textFormat_linear = 22.2
  textRenderer_color = rgb(0,0,0)
  textRenderer_family = inherit
  textRenderer_size = 3.6
  unit_custom_scale = 1
  unit_scheme = 0
FEATURE [Drawing::FeatureViewPython] dim011  # drawing view (typed FeaturePython)
  Rotation = 0
  ViewResult = <g> \n  <line x1="78.000000" y1="91.000000" x2="86.774706" y2="91.000000" style="stroke:rgb(255,0,0);stroke-width:0.10" />\n<line x1="78.000000" y1="72.000000" x2="86.774706" y2="72.000000" style="stroke:rgb(255,0,0);stroke-width:0.10" />\n<line x1="85.774706" y1="91.000000" x2="85.774706" y2="72.000000" style="stroke:rgb(255,0,0);stroke-width:0.10" /> \n  <polygon points="85.774706,72.000000 85.274706,74.000000 85.774706,74.500000 86.274706,74.000000" style="fill:rgb(255,0,0);stroke:rgb(255,0,0);stroke-width:0" /><polygon points="85.774706,91.000000 86.274706,89.000000 85.774706,88.500000 85.274706,89.000000" style="fill:rgb(255,0,0);stroke:rgb(255,0,0);stroke-width:0" /> \n  <text x="83.774706" y="81.500000" font-family="inherit" font-size="3.6" fill="rgb(0,0,0)" text-anchor="middle" transform="rotate(-90.000000 83.774706,81.500000)" >19</text> </g>
  Visible = false
  X = 0
  Y = 0
  arrowL1 = 2
  arrowL2 = 0.5
  arrowW = 1
  arrow_scheme = 0
  autoPlaceOffset = 2
  autoPlaceText = true
  click1_x = 85.7747
  click1_y = 75.3485
  click2_x = 85.7747
  click2_y = 75.3485
  comma_decimal_place = false
  dimension_line_overshoot = 1
  gap_datum_points = 0
  halfDimension_linear = false
  lineColor = rgb(255,0,0)
  strokeWidth = 0.1
  textFormat_linear = %(value)3.3f
  textRenderer_color = rgb(0,0,0)
  textRenderer_family = inherit
  textRenderer_size = 3.6
  unit_custom_scale = 1
  unit_scheme = 0
FEATURE [Drawing::FeatureViewPython] dim012  # drawing view (typed FeaturePython)
  Rotation = 0
  ViewResult = <g> \n  <line x1="247.939250" y1="70.400000" x2="259.452952" y2="70.400000" style="stroke:rgb(255,0,0);stroke-width:0.10" />\n<line x1="247.650250" y1="92.600000" x2="259.452952" y2="92.600000" style="stroke:rgb(255,0,0);stroke-width:0.10" />\n<line x1="258.452952" y1="70.400000" x2="258.452952" y2="92.600000" style="stroke:rgb(255,0,0);stroke-width:0.10" /> \n  <polygon points="258.452952,92.600000 258.952952,90.600000 258.452952,90.100000 257.952952,90.600000" style="fill:rgb(255,0,0);stroke:rgb(255,0,0);stroke-width:0" /><polygon points="258.452952,70.400000 257.952952,72.400000 258.452952,72.900000 258.952952,72.400000" style="fill:rgb(255,0,0);stroke:rgb(255,0,0);stroke-width:0" /> \n  <text x="256.452952" y="81.500000" font-family="inherit" font-size="3.6" fill="rgb(0,0,0)" text-anchor="middle" transform="rotate(-90.000000 256.452952,81.500000)" >22.2</text> </g>
  Visible = false
  X = 0
  Y = 0
  arrowL1 = 2
  arrowL2 = 0.5
  arrowW = 1
  arrow_scheme = 0
  autoPlaceOffset = 2
  autoPlaceText = true
  click1_x = 258.453
  click1_y = 91.9892
  click2_x = 258.453
  click2_y = 91.9892
  comma_decimal_place = false
  dimension_line_overshoot = 1
  gap_datum_points = 0
  halfDimension_linear = false
  lineColor = rgb(255,0,0)
  strokeWidth = 0.1
  textFormat_linear = %(value)3.3f
  textRenderer_color = rgb(0,0,0)
  textRenderer_family = inherit
  textRenderer_size = 3.6
  unit_custom_scale = 1
  unit_scheme = 0
FEATURE [Drawing::FeatureViewPython] dim013  # drawing view (typed FeaturePython)
  Rotation = 0
  ViewResult = <g> \n  <line x1="233.000000" y1="92.844700" x2="233.000000" y2="103.971074" style="stroke:rgb(255,0,0);stroke-width:0.10" />\n<line x1="248.000000" y1="94.000000" x2="248.000000" y2="103.971074" style="stroke:rgb(255,0,0);stroke-width:0.10" />\n<line x1="233.000000" y1="102.971074" x2="248.000000" y2="102.971074" style="stroke:rgb(255,0,0);stroke-width:0.10" /> \n  <polygon points="248.000000,102.971074 246.000000,102.471074 245.500000,102.971074 246.000000,103.471074" style="fill:rgb(255,0,0);stroke:rgb(255,0,0);stroke-width:0" /><polygon points="233.000000,102.971074 235.000000,103.471074 235.500000,102.971074 235.000000,102.471074" style="fill:rgb(255,0,0);stroke:rgb(255,0,0);stroke-width:0" /> \n  <text x="240.500000" y="100.971074" font-family="inherit" font-size="3.6" fill="rgb(0,0,0)" text-anchor="middle" transform="rotate(0.000000 240.500000,100.971074)" >15</text> </g>
  Visible = false
  X = 0
  Y = 0
  arrowL1 = 2
  arrowL2 = 0.5
  arrowW = 1
  arrow_scheme = 0
  autoPlaceOffset = 2
  autoPlaceText = true
  click1_x = 245.65
  click1_y = 102.971
  click2_x = 245.65
  click2_y = 102.971
  comma_decimal_place = false
  dimension_line_overshoot = 1
  gap_datum_points = 0
  halfDimension_linear = false
  lineColor = rgb(255,0,0)
  strokeWidth = 0.1
  textFormat_linear = %(value)3.3f
  textRenderer_color = rgb(0,0,0)
  textRenderer_family = inherit
  textRenderer_size = 3.6
  unit_custom_scale = 1
  unit_scheme = 0
FEATURE [Drawing::FeatureViewPython] dim014  # drawing view (typed FeaturePython)
  Rotation = 0
  ViewResult = <g> \n  <line x1="247.650250" y1="92.600000" x2="259.470256" y2="92.600000" style="stroke:rgb(255,0,0);stroke-width:0.10" />\n<line x1="247.881190" y1="93.000000" x2="259.470256" y2="93.000000" style="stroke:rgb(255,0,0);stroke-width:0.10" />\n<line x1="258.470256" y1="92.600000" x2="258.470256" y2="93.000000" style="stroke:rgb(255,0,0);stroke-width:0.10" /> \n  <polygon points="258.470256,93.000000 257.970256,95.000000 258.470256,95.500000 258.970256,95.000000" style="fill:rgb(255,0,0);stroke:rgb(255,0,0);stroke-width:0" /><polygon points="258.470256,92.600000 258.970256,90.600000 258.470256,90.100000 257.970256,90.600000" style="fill:rgb(255,0,0);stroke:rgb(255,0,0);stroke-width:0" /> \n  <text x="256.470256" y="92.800000" font-family="inherit" font-size="3.6" fill="rgb(0,0,0)" text-anchor="middle" transform="rotate(-90.000000 256.470256,92.800000)" >0.4</text> </g>
  Visible = false
  X = 0
  Y = 0
  arrowL1 = 2
  arrowL2 = 0.5
  arrowW = 1
  arrow_scheme = 0
  autoPlaceOffset = 2
  autoPlaceText = true
  click1_x = 258.47
  click1_y = 92.613
  click2_x = 258.47
  click2_y = 92.613
  comma_decimal_place = false
  dimension_line_overshoot = 1
  gap_datum_points = 0
  halfDimension_linear = false
  lineColor = rgb(255,0,0)
  strokeWidth = 0.1
  textFormat_linear = %(value)3.3f
  textRenderer_color = rgb(0,0,0)
  textRenderer_family = inherit
  textRenderer_size = 3.6
  unit_custom_scale = 1
  unit_scheme = 0
FEATURE [Drawing::FeatureViewPython] dim015  # drawing view (typed FeaturePython)
  Rotation = 0
  ViewResult = <g> \n  <line x1="248.000000" y1="69.000000" x2="259.424014" y2="69.000000" style="stroke:rgb(255,0,0);stroke-width:0.10" />\n<line x1="233.000000" y1="70.400000" x2="259.424014" y2="70.400000" style="stroke:rgb(255,0,0);stroke-width:0.10" />\n<line x1="258.424014" y1="69.000000" x2="258.424014" y2="70.400000" style="stroke:rgb(255,0,0);stroke-width:0.10" /> \n  <polygon points="258.424014,70.400000 257.924014,72.400000 258.424014,72.900000 258.924014,72.400000" style="fill:rgb(255,0,0);stroke:rgb(255,0,0);stroke-width:0" /><polygon points="258.424014,69.000000 258.924014,67.000000 258.424014,66.500000 257.924014,67.000000" style="fill:rgb(255,0,0);stroke:rgb(255,0,0);stroke-width:0" /> \n  <text x="256.424014" y="69.700000" font-family="inherit" font-size="3.6" fill="rgb(0,0,0)" text-anchor="middle" transform="rotate(-90.000000 256.424014,69.700000)" >1.4</text> </g>
  Visible = false
  X = 0
  Y = 0
  arrowL1 = 2
  arrowL2 = 0.5
  arrowW = 1
  arrow_scheme = 0
  autoPlaceOffset = 2
  autoPlaceText = true
  click1_x = 258.424
  click1_y = 69.2695
  click2_x = 258.424
  click2_y = 69.2695
  comma_decimal_place = false
  dimension_line_overshoot = 1
  gap_datum_points = 0
  halfDimension_linear = false
  lineColor = rgb(255,0,0)
  strokeWidth = 0.1
  textFormat_linear = %(value)3.3f
  textRenderer_color = rgb(0,0,0)
  textRenderer_family = inherit
  textRenderer_size = 3.6
  unit_custom_scale = 1
  unit_scheme = 0
FEATURE [Drawing::FeatureViewPython] dim016  # drawing view (typed FeaturePython)
  Rotation = 0
  ViewResult = <g> \n  <line x1="247.650250" y1="92.600000" x2="247.650250" y2="88.519925" style="stroke:rgb(255,0,0);stroke-width:0.10" />\n<line x1="247.072250" y1="92.600000" x2="247.072250" y2="88.519925" style="stroke:rgb(255,0,0);stroke-width:0.10" />\n<line x1="247.650250" y1="89.519925" x2="247.072250" y2="89.519925" style="stroke:rgb(255,0,0);stroke-width:0.10" /> \n  <polygon points="247.072250,89.519925 245.072250,89.019925 244.572250,89.519925 245.072250,90.019925" style="fill:rgb(255,0,0);stroke:rgb(255,0,0);stroke-width:0" /><polygon points="247.650250,89.519925 249.650250,90.019925 250.150250,89.519925 249.650250,89.019925" style="fill:rgb(255,0,0);stroke:rgb(255,0,0);stroke-width:0" /> \n  <text x="247.361250" y="87.519925" font-family="inherit" font-size="3.6" fill="rgb(0,0,0)" text-anchor="middle" transform="rotate(0.000000 247.361250,87.519925)" >0.578</text> </g>
  Visible = false
  X = 0
  Y = 0
  arrowL1 = 2
  arrowL2 = 0.5
  arrowW = 1
  arrow_scheme = 0
  autoPlaceOffset = 2
  autoPlaceText = true
  click1_x = 247.628
  click1_y = 89.5199
  click2_x = 247.628
  click2_y = 89.5199
  comma_decimal_place = false
  dimension_line_overshoot = 1
  gap_datum_points = 0
  halfDimension_linear = false
  lineColor = rgb(255,0,0)
  strokeWidth = 0.1
  textFormat_linear = %(value)3.3f
  textRenderer_color = rgb(0,0,0)
  textRenderer_family = inherit
  textRenderer_size = 3.6
  unit_custom_scale = 1
  unit_scheme = 0
FEATURE [Drawing::FeatureViewPython] dim017  # drawing view (typed FeaturePython)
  Rotation = 0
  ViewResult = <g> \n  <line x1="74.825000" y1="91.200000" x2="74.825000" y2="86.245403" style="stroke:rgb(255,0,0);stroke-width:0.10" />\n<line x1="73.439000" y1="91.200000" x2="73.439000" y2="86.245403" style="stroke:rgb(255,0,0);stroke-width:0.10" />\n<line x1="74.825000" y1="87.245403" x2="73.439000" y2="87.245403" style="stroke:rgb(255,0,0);stroke-width:0.10" /> \n  <polygon points="73.439000,87.245403 71.439000,86.745403 70.939000,87.245403 71.439000,87.745403" style="fill:rgb(255,0,0);stroke:rgb(255,0,0);stroke-width:0" /><polygon points="74.825000,87.245403 76.825000,87.745403 77.325000,87.245403 76.825000,86.745403" style="fill:rgb(255,0,0);stroke:rgb(255,0,0);stroke-width:0" /> \n  <text x="74.132000" y="85.245403" font-family="inherit" font-size="3.6" fill="rgb(0,0,0)" text-anchor="middle" transform="rotate(0.000000 74.132000,85.245403)" >1.386</text> </g>
  Visible = false
  X = 0
  Y = 0
  arrowL1 = 2
  arrowL2 = 0.5
  arrowW = 1
  arrow_scheme = 0
  autoPlaceOffset = 2
  autoPlaceText = true
  click1_x = 74.579
  click1_y = 87.2454
  click2_x = 74.579
  click2_y = 87.2454
  comma_decimal_place = false
  dimension_line_overshoot = 1
  gap_datum_points = 0
  halfDimension_linear = false
  lineColor = rgb(255,0,0)
  strokeWidth = 0.1
  textFormat_linear = %(value)3.3f
  textRenderer_color = rgb(0,0,0)
  textRenderer_family = inherit
  textRenderer_size = 3.6
  unit_custom_scale = 1
  unit_scheme = 0
FEATURE [Drawing::FeatureViewPython] dim018  # drawing view (typed FeaturePython)
  Rotation = 0
  ViewResult = <g> \n  <line x1="62.239000" y1="91.200000" x2="43.849934" y2="91.200000" style="stroke:rgb(255,0,0);stroke-width:0.10" />\n<line x1="62.931000" y1="92.200000" x2="43.849934" y2="92.200000" style="stroke:rgb(255,0,0);stroke-width:0.10" />\n<line x1="44.849934" y1="91.200000" x2="44.849934" y2="92.200000" style="stroke:rgb(255,0,0);stroke-width:0.10" /> \n  <polygon points="44.849934,92.200000 44.349934,94.200000 44.849934,94.700000 45.349934,94.200000" style="fill:rgb(255,0,0);stroke:rgb(255,0,0);stroke-width:0" /><polygon points="44.849934,91.200000 45.349934,89.200000 44.849934,88.700000 44.349934,89.200000" style="fill:rgb(255,0,0);stroke:rgb(255,0,0);stroke-width:0" /> \n  <text x="42.849934" y="91.700000" font-family="inherit" font-size="3.6" fill="rgb(0,0,0)" text-anchor="middle" transform="rotate(-90.000000 42.849934,91.700000)" >1</text> </g>
  Visible = false
  X = 0
  Y = 0
  arrowL1 = 2
  arrowL2 = 0.5
  arrowW = 1
  arrow_scheme = 0
  autoPlaceOffset = 2
  autoPlaceText = true
  click1_x = 44.8499
  click1_y = 91.4785
  click2_x = 44.8499
  click2_y = 91.4785
  comma_decimal_place = false
  dimension_line_overshoot = 1
  gap_datum_points = 0
  halfDimension_linear = false
  lineColor = rgb(255,0,0)
  strokeWidth = 0.1
  textFormat_linear = %(value)3.3f
  textRenderer_color = rgb(0,0,0)
  textRenderer_family = inherit
  textRenderer_size = 3.6
  unit_custom_scale = 1
  unit_scheme = 0
FEATURE [Drawing::FeatureViewPython] dim019  # drawing view (typed FeaturePython)
  Rotation = 0
  ViewResult = <g> \n  <line x1="62.239000" y1="70.800000" x2="43.895994" y2="70.800000" style="stroke:rgb(255,0,0);stroke-width:0.10" />\n<line x1="61.661000" y1="71.800000" x2="43.895994" y2="71.800000" style="stroke:rgb(255,0,0);stroke-width:0.10" />\n<line x1="44.895994" y1="70.800000" x2="44.895994" y2="71.800000" style="stroke:rgb(255,0,0);stroke-width:0.10" /> \n  <polygon points="44.895994,71.800000 44.395994,73.800000 44.895994,74.300000 45.395994,73.800000" style="fill:rgb(255,0,0);stroke:rgb(255,0,0);stroke-width:0" /><polygon points="44.895994,70.800000 45.395994,68.800000 44.895994,68.300000 44.395994,68.800000" style="fill:rgb(255,0,0);stroke:rgb(255,0,0);stroke-width:0" /> \n  <text x="42.895994" y="71.300000" font-family="inherit" font-size="3.6" fill="rgb(0,0,0)" text-anchor="middle" transform="rotate(-90.000000 42.895994,71.300000)" >1</text> </g>
  Visible = false
  X = 0
  Y = 0
  arrowL1 = 2
  arrowL2 = 0.5
  arrowW = 1
  arrow_scheme = 0
  autoPlaceOffset = 2
  autoPlaceText = true
  click1_x = 44.896
  click1_y = 71.5818
  click2_x = 44.896
  click2_y = 71.5818
  comma_decimal_place = false
  dimension_line_overshoot = 1
  gap_datum_points = 0
  halfDimension_linear = false
  lineColor = rgb(255,0,0)
  strokeWidth = 0.1
  textFormat_linear = %(value)3.3f
  textRenderer_color = rgb(0,0,0)
  textRenderer_family = inherit
  textRenderer_size = 3.6
  unit_custom_scale = 1
  unit_scheme = 0
FEATURE [Drawing::FeatureViewPython] dim001  # drawing view (typed FeaturePython)
  Rotation = 0
  ViewResult = <g> \n  <line x1="248.000000" y1="69.000000" x2="248.000000" y2="51.037466" style="stroke:rgb(255,0,0);stroke-width:0.10" />\n<line x1="49.000000" y1="69.000000" x2="49.000000" y2="51.037466" style="stroke:rgb(255,0,0);stroke-width:0.10" />\n<line x1="248.000000" y1="52.037466" x2="49.000000" y2="52.037466" style="stroke:rgb(255,0,0);stroke-width:0.10" /> \n  <polygon points="49.000000,52.037466 51.000000,52.537466 51.500000,52.037466 51.000000,51.537466" style="fill:rgb(255,0,0);stroke:rgb(255,0,0);stroke-width:0" /><polygon points="248.000000,52.037466 246.000000,51.537466 245.500000,52.037466 246.000000,52.537466" style="fill:rgb(255,0,0);stroke:rgb(255,0,0);stroke-width:0" /> \n  <text x="148.500000" y="50.037466" font-family="inherit" font-size="3.6" fill="rgb(0,0,0)" text-anchor="middle" transform="rotate(0.000000 148.500000,50.037466)" >199</text> </g>
  Visible = false
  X = 0
  Y = 0
  arrowL1 = 2
  arrowL2 = 0.5
  arrowW = 1
  arrow_scheme = 0
  autoPlaceOffset = 2
  autoPlaceText = true
  click1_x = 159.634
  click1_y = 52.0375
  click2_x = 159.634
  click2_y = 52.0375
  comma_decimal_place = false
  dimension_line_overshoot = 1
  gap_datum_points = 0
  halfDimension_linear = false
  lineColor = rgb(255,0,0)
  strokeWidth = 0.1
  textFormat_linear = %(value)3.3f
  textRenderer_color = rgb(0,0,0)
  textRenderer_family = inherit
  textRenderer_size = 3.6
  unit_custom_scale = 1
  unit_scheme = 0
FEATURE [Drawing::FeaturePage] Page010  label="BatteryHolderCrossSction"
  EditableTexts = Dr. Zoidberg | 13.02.2019 | x1.0 | ??? | ERG-T-01 | Battery Holder. Cross Section. | Part #2 | Sheet #2
  Group = -> [Ortho025,dim002,dim003,dim004,dim005,dim006,dim007,dim008,dim009,dim010,dim011,dim012,dim013,dim014,dim015,dim016,dim017,dim018,dim019,dim001]
  Template = <path>
FEATURE [Drawing::FeatureViewPython] dia001  # drawing view (typed FeaturePython)
  Rotation = 0
  ViewResult = <g>  <circle cx ="41.937500" cy ="81.500000" r="0.250000" stroke="none" fill="rgb(255,0,0)" /> \n<line x1="23.590175" y1="110.087484" x2="47.001175" y2="73.610145" style="stroke:rgb(255,0,0);stroke-width:0.10" />\n<polygon points="36.873825,89.389855 38.374868,87.976749 38.224138,87.285894 37.533283,87.436623" style="fill:rgb(255,0,0);stroke:rgb(255,0,0);stroke-width:0" />\n<polygon points="47.001175,73.610145 45.500132,75.023251 45.650862,75.714106 46.341717,75.563377" style="fill:rgb(255,0,0);stroke:rgb(255,0,0);stroke-width:0" />\n<line x1="23.590175" y1="110.087484" x2="15.887261" y2="110.087484" style="stroke:rgb(255,0,0);stroke-width:0.10" />\n<text x="19.738718" y="108.087484" font-family="inherit" font-size="3.6" fill="rgb(0,0,0)" text-anchor="middle" transform="rotate(0.000000 19.738718,108.087484)" >Ø25</text> </g>
  Visible = false
  X = 0
  Y = 0
  arrowL1 = 2
  arrowL2 = 0.5
  arrowW = 1
  arrow_scheme = 0
  autoPlaceOffset = 2
  autoPlaceText = true
  centerPointDia = 0.5
  click1_x = 23.5902
  click1_y = 110.087
  click2_x = 15.8873
  click2_y = 110.408
  click3_x = 15.8873
  click3_y = 110.408
  comma_decimal_place = false
  lineColor = rgb(255,0,0)
  strokeWidth = 0.1
  textFormat_circular = Ø%(value)3.3f
  textRenderer_color = rgb(0,0,0)
  textRenderer_family = inherit
  textRenderer_size = 3.6
  unit_custom_scale = 1
  unit_scheme = 0
FEATURE [Drawing::FeatureViewPython] dia002  # drawing view (typed FeaturePython)
  Rotation = 0
  ViewResult = <g>  <circle cx ="41.937500" cy ="81.500000" r="0.250000" stroke="none" fill="rgb(255,0,0)" /> \n<line x1="27.345346" y1="119.202599" x2="44.509215" y2="74.855310" style="stroke:rgb(255,0,0);stroke-width:0.10" />\n<polygon points="39.365785,88.144690 40.553964,86.459985 40.268141,85.813220 39.621376,86.099043" style="fill:rgb(255,0,0);stroke:rgb(255,0,0);stroke-width:0" />\n<polygon points="44.509215,74.855310 43.321036,76.540015 43.606859,77.186780 44.253624,76.900957" style="fill:rgb(255,0,0);stroke:rgb(255,0,0);stroke-width:0" />\n<line x1="27.345346" y1="119.202599" x2="16.946411" y2="119.202599" style="stroke:rgb(255,0,0);stroke-width:0.10" />\n<text x="22.145879" y="117.202599" font-family="inherit" font-size="3.6" fill="rgb(0,0,0)" text-anchor="middle" transform="rotate(0.000000 22.145879,117.202599)" >Ø19</text> </g>
  Visible = false
  X = 0
  Y = 0
  arrowL1 = 2
  arrowL2 = 0.5
  arrowW = 1
  arrow_scheme = 0
  autoPlaceOffset = 2
  autoPlaceText = true
  centerPointDia = 0.5
  click1_x = 27.3453
  click1_y = 119.203
  click2_x = 16.9464
  click2_y = 120.936
  click3_x = 16.9464
  click3_y = 120.936
  comma_decimal_place = false
  lineColor = rgb(255,0,0)
  strokeWidth = 0.1
  textFormat_circular = Ø%(value)3.3f
  textRenderer_color = rgb(0,0,0)
  textRenderer_family = inherit
  textRenderer_size = 3.6
  unit_custom_scale = 1
  unit_scheme = 0
FEATURE [Drawing::FeatureViewPython] dia003  # drawing view (typed FeaturePython)
  Rotation = 0
  ViewResult = <g>  <circle cx ="255.062000" cy ="81.500000" r="0.250000" stroke="none" fill="rgb(255,0,0)" /> \n<line x1="274.737029" y1="106.863676" x2="249.315824" y2="74.092431" style="stroke:rgb(255,0,0);stroke-width:0.10" />\n<polygon points="260.808176,88.907569 259.977396,87.020825 259.275862,86.932218 259.187255,87.633751" style="fill:rgb(255,0,0);stroke:rgb(255,0,0);stroke-width:0" />\n<polygon points="249.315824,74.092431 250.146604,75.979175 250.848138,76.067782 250.936745,75.366249" style="fill:rgb(255,0,0);stroke:rgb(255,0,0);stroke-width:0" />\n<line x1="274.737029" y1="106.863676" x2="285.007829" y2="106.863676" style="stroke:rgb(255,0,0);stroke-width:0.10" />\n<text x="279.872429" y="104.863676" font-family="inherit" font-size="3.6" fill="rgb(0,0,0)" text-anchor="middle" transform="rotate(0.000000 279.872429,104.863676)" >Ø25</text> </g>
  Visible = false
  X = 0
  Y = 0
  arrowL1 = 2
  arrowL2 = 0.5
  arrowW = 1
  arrow_scheme = 0
  autoPlaceOffset = 2
  autoPlaceText = true
  centerPointDia = 0.5
  click1_x = 274.737
  click1_y = 106.864
  click2_x = 285.008
  click2_y = 105.722
  click3_x = 285.008
  click3_y = 105.722
  comma_decimal_place = false
  lineColor = rgb(255,0,0)
  strokeWidth = 0.1
  textFormat_circular = Ø%(value)3.3f
  textRenderer_color = rgb(0,0,0)
  textRenderer_family = inherit
  textRenderer_size = 3.6
  unit_custom_scale = 1
  unit_scheme = 0
FEATURE [Drawing::FeatureViewPython] dia004  # drawing view (typed FeaturePython)
  Rotation = 0
  ViewResult = <g>  <circle cx ="255.062000" cy ="81.500000" r="0.250000" stroke="none" fill="rgb(255,0,0)" /> \n<line x1="269.844041" y1="118.221575" x2="252.401354" y2="74.890417" style="stroke:rgb(255,0,0);stroke-width:0.10" />\n<polygon points="257.722646,88.109583 257.439629,86.067549 256.789086,85.790431 256.511968,86.440973" style="fill:rgb(255,0,0);stroke:rgb(255,0,0);stroke-width:0" />\n<polygon points="252.401354,74.890417 252.684371,76.932451 253.334914,77.209569 253.612032,76.559027" style="fill:rgb(255,0,0);stroke:rgb(255,0,0);stroke-width:0" />\n<line x1="269.844041" y1="118.221575" x2="278.926740" y2="118.221575" style="stroke:rgb(255,0,0);stroke-width:0.10" />\n<text x="274.385390" y="116.221575" font-family="inherit" font-size="3.6" fill="rgb(0,0,0)" text-anchor="middle" transform="rotate(0.000000 274.385390,116.221575)" >Ø19</text> </g>
  Visible = false
  X = 0
  Y = 0
  arrowL1 = 2
  arrowL2 = 0.5
  arrowW = 1
  arrow_scheme = 0
  autoPlaceOffset = 2
  autoPlaceText = true
  centerPointDia = 0.5
  click1_x = 269.844
  click1_y = 118.222
  click2_x = 278.927
  click2_y = 119.98
  click3_x = 278.927
  click3_y = 119.98
  comma_decimal_place = false
  lineColor = rgb(255,0,0)
  strokeWidth = 0.1
  textFormat_circular = Ø%(value)3.3f
  textRenderer_color = rgb(0,0,0)
  textRenderer_family = inherit
  textRenderer_size = 3.6
  unit_custom_scale = 1
  unit_scheme = 0
FEATURE [Drawing::FeatureViewPython] dia005  # drawing view (typed FeaturePython)
  Rotation = 0
  ViewResult = <g>  <circle cx ="255.059998" cy ="81.501557" r="0.250000" stroke="none" fill="rgb(255,0,0)" /> \n<line x1="266.236434" y1="47.920329" x2="252.430269" y2="89.402960" style="stroke:rgb(255,0,0);stroke-width:0.10" />\n<polygon points="257.689727,73.600153 256.583737,75.339919 256.900258,75.972228 257.532566,75.655707" style="fill:rgb(255,0,0);stroke:rgb(255,0,0);stroke-width:0" />\n<polygon points="252.430269,89.402960 253.536259,87.663194 253.219738,87.030885 252.587429,87.347406" style="fill:rgb(255,0,0);stroke:rgb(255,0,0);stroke-width:0" />\n<line x1="266.236434" y1="47.920329" x2="280.946860" y2="47.920329" style="stroke:rgb(255,0,0);stroke-width:0.10" />\n<text x="273.591647" y="45.920329" font-family="inherit" font-size="3.6" fill="rgb(0,0,0)" text-anchor="middle" transform="rotate(0.000000 273.591647,45.920329)" >Ø22.2</text> </g>
  Visible = false
  X = 0
  Y = 0
  arrowL1 = 2
  arrowL2 = 0.5
  arrowW = 1
  arrow_scheme = 0
  autoPlaceOffset = 2
  autoPlaceText = true
  centerPointDia = 0.5
  click1_x = 266.236
  click1_y = 47.9203
  click2_x = 280.947
  click2_y = 49.592
  click3_x = 280.947
  click3_y = 49.592
  comma_decimal_place = false
  lineColor = rgb(255,0,0)
  strokeWidth = 0.1
  textFormat_circular = Ø%(value)3.1f
  textRenderer_color = rgb(0,0,0)
  textRenderer_family = inherit
  textRenderer_size = 3.6
  unit_custom_scale = 1
  unit_scheme = 0
FEATURE [Drawing::FeatureViewPython] dim020  # drawing view (typed FeaturePython)
  Rotation = 0
  ViewResult = <g> \n  <line x1="223.125000" y1="72.125000" x2="223.125000" y2="50.789519" style="stroke:rgb(255,0,0);stroke-width:0.10" />\n<line x1="73.875000" y1="72.125000" x2="73.875000" y2="50.789519" style="stroke:rgb(255,0,0);stroke-width:0.10" />\n<line x1="223.125000" y1="51.789519" x2="73.875000" y2="51.789519" style="stroke:rgb(255,0,0);stroke-width:0.10" /> \n  <polygon points="73.875000,51.789519 75.875000,52.289519 76.375000,51.789519 75.875000,51.289519" style="fill:rgb(255,0,0);stroke:rgb(255,0,0);stroke-width:0" /><polygon points="223.125000,51.789519 221.125000,51.289519 220.625000,51.789519 221.125000,52.289519" style="fill:rgb(255,0,0);stroke:rgb(255,0,0);stroke-width:0" /> \n  <text x="148.500000" y="49.789519" font-family="inherit" font-size="3.6" fill="rgb(0,0,0)" text-anchor="middle" transform="rotate(0.000000 148.500000,49.789519)" >199</text> </g>
  Visible = false
  X = 0
  Y = 0
  arrowL1 = 2
  arrowL2 = 0.5
  arrowW = 1
  arrow_scheme = 0
  autoPlaceOffset = 2
  autoPlaceText = true
  click1_x = 131.706
  click1_y = 51.7895
  click2_x = 131.706
  click2_y = 51.7895
  comma_decimal_place = false
  dimension_line_overshoot = 1
  gap_datum_points = 0
  halfDimension_linear = false
  lineColor = rgb(255,0,0)
  strokeWidth = 0.1
  textFormat_linear = %(value)3.3f
  textRenderer_color = rgb(0,0,0)
  textRenderer_family = inherit
  textRenderer_size = 3.6
  unit_custom_scale = 1
  unit_scheme = 0
FEATURE [Drawing::FeatureViewPython] dim021  # drawing view (typed FeaturePython)
  Rotation = 0
  ViewResult = <g> \n  <line x1="83.250000" y1="73.475000" x2="83.250000" y2="64.528585" style="stroke:rgb(255,0,0);stroke-width:0.10" />\n<line x1="73.875000" y1="73.475000" x2="73.875000" y2="64.528585" style="stroke:rgb(255,0,0);stroke-width:0.10" />\n<line x1="83.250000" y1="65.528585" x2="73.875000" y2="65.528585" style="stroke:rgb(255,0,0);stroke-width:0.10" /> \n  <polygon points="73.875000,65.528585 75.875000,66.028585 76.375000,65.528585 75.875000,65.028585" style="fill:rgb(255,0,0);stroke:rgb(255,0,0);stroke-width:0" /><polygon points="83.250000,65.528585 81.250000,65.028585 80.750000,65.528585 81.250000,66.028585" style="fill:rgb(255,0,0);stroke:rgb(255,0,0);stroke-width:0" /> \n  <text x="78.562500" y="63.528585" font-family="inherit" font-size="3.6" fill="rgb(0,0,0)" text-anchor="middle" transform="rotate(0.000000 78.562500,63.528585)" >12.5</text> </g>
  Visible = false
  X = 0
  Y = 0
  arrowL1 = 2
  arrowL2 = 0.5
  arrowW = 1
  arrow_scheme = 0
  autoPlaceOffset = 2
  autoPlaceText = true
  click1_x = 80.8839
  click1_y = 65.5286
  click2_x = 80.8839
  click2_y = 65.5286
  comma_decimal_place = false
  dimension_line_overshoot = 1
  gap_datum_points = 0
  halfDimension_linear = false
  lineColor = rgb(255,0,0)
  strokeWidth = 0.1
  textFormat_linear = %(value)3.3f
  textRenderer_color = rgb(0,0,0)
  textRenderer_family = inherit
  textRenderer_size = 3.6
  unit_custom_scale = 1
  unit_scheme = 0
FEATURE [Drawing::FeatureViewPython] dim022  # drawing view (typed FeaturePython)
  Rotation = 0
  ViewResult = <g> \n  <line x1="83.250000" y1="73.475000" x2="83.250000" y2="64.525210" style="stroke:rgb(255,0,0);stroke-width:0.10" />\n<line x1="94.200000" y1="74.375000" x2="94.200000" y2="64.525210" style="stroke:rgb(255,0,0);stroke-width:0.10" />\n<line x1="83.250000" y1="65.525210" x2="94.200000" y2="65.525210" style="stroke:rgb(255,0,0);stroke-width:0.10" /> \n  <polygon points="94.200000,65.525210 92.200000,65.025210 91.700000,65.525210 92.200000,66.025210" style="fill:rgb(255,0,0);stroke:rgb(255,0,0);stroke-width:0" /><polygon points="83.250000,65.525210 85.250000,66.025210 85.750000,65.525210 85.250000,65.025210" style="fill:rgb(255,0,0);stroke:rgb(255,0,0);stroke-width:0" /> \n  <text x="88.725000" y="63.525210" font-family="inherit" font-size="3.6" fill="rgb(0,0,0)" text-anchor="middle" transform="rotate(0.000000 88.725000,63.525210)" >14.6</text> </g>
  Visible = false
  X = 0
  Y = 0
  arrowL1 = 2
  arrowL2 = 0.5
  arrowW = 1
  arrow_scheme = 0
  autoPlaceOffset = 2
  autoPlaceText = true
  click1_x = 91.3621
  click1_y = 65.5252
  click2_x = 91.3621
  click2_y = 65.5252
  comma_decimal_place = false
  dimension_line_overshoot = 1
  gap_datum_points = 0
  halfDimension_linear = false
  lineColor = rgb(255,0,0)
  strokeWidth = 0.1
  textFormat_linear = %(value)3.3f
  textRenderer_color = rgb(0,0,0)
  textRenderer_family = inherit
  textRenderer_size = 3.6
  unit_custom_scale = 1
  unit_scheme = 0
FEATURE [Drawing::FeatureViewPython] dim024  # drawing view (typed FeaturePython)
  Rotation = 0
  ViewResult = <g> \n  <line x1="95.625000" y1="88.625000" x2="95.625000" y2="99.470468" style="stroke:rgb(255,0,0);stroke-width:0.10" />\n<line x1="94.200000" y1="88.625000" x2="94.200000" y2="99.470468" style="stroke:rgb(255,0,0);stroke-width:0.10" />\n<line x1="95.625000" y1="98.470468" x2="94.200000" y2="98.470468" style="stroke:rgb(255,0,0);stroke-width:0.10" /> \n  <polygon points="94.200000,98.470468 92.200000,97.970468 91.700000,98.470468 92.200000,98.970468" style="fill:rgb(255,0,0);stroke:rgb(255,0,0);stroke-width:0" /><polygon points="95.625000,98.470468 97.625000,98.970468 98.125000,98.470468 97.625000,97.970468" style="fill:rgb(255,0,0);stroke:rgb(255,0,0);stroke-width:0" /> \n  <text x="94.912500" y="96.470468" font-family="inherit" font-size="3.6" fill="rgb(0,0,0)" text-anchor="middle" transform="rotate(-0.000000 94.912500,96.470468)" >1.9</text> </g>
  Visible = false
  X = 0
  Y = 0
  arrowL1 = 2
  arrowL2 = 0.5
  arrowW = 1
  arrow_scheme = 0
  autoPlaceOffset = 2
  autoPlaceText = true
  click1_x = 94.0154
  click1_y = 98.4705
  click2_x = 94.0154
  click2_y = 98.4705
  comma_decimal_place = false
  dimension_line_overshoot = 1
  gap_datum_points = 0
  halfDimension_linear = false
  lineColor = rgb(255,0,0)
  strokeWidth = 0.1
  textFormat_linear = %(value)3.3f
  textRenderer_color = rgb(0,0,0)
  textRenderer_family = inherit
  textRenderer_size = 3.6
  unit_custom_scale = 1
  unit_scheme = 0
FEATURE [Drawing::FeatureViewPython] dim023  # drawing view (typed FeaturePython)
  Rotation = 0
  ViewResult = <g> \n  <line x1="95.625000" y1="73.175000" x2="95.625000" y2="64.528264" style="stroke:rgb(255,0,0);stroke-width:0.10" />\n<line x1="211.875000" y1="73.180175" x2="211.875000" y2="64.528264" style="stroke:rgb(255,0,0);stroke-width:0.10" />\n<line x1="95.625000" y1="65.528264" x2="211.875000" y2="65.528264" style="stroke:rgb(255,0,0);stroke-width:0.10" /> \n  <polygon points="211.875000,65.528264 209.875000,65.028264 209.375000,65.528264 209.875000,66.028264" style="fill:rgb(255,0,0);stroke:rgb(255,0,0);stroke-width:0" /><polygon points="95.625000,65.528264 97.625000,66.028264 98.125000,65.528264 97.625000,65.028264" style="fill:rgb(255,0,0);stroke:rgb(255,0,0);stroke-width:0" /> \n  <text x="153.750000" y="63.528264" font-family="inherit" font-size="3.6" fill="rgb(0,0,0)" text-anchor="middle" transform="rotate(0.000000 153.750000,63.528264)" >155</text> </g>
  Visible = false
  X = 0
  Y = 0
  arrowL1 = 2
  arrowL2 = 0.5
  arrowW = 1
  arrow_scheme = 0
  autoPlaceOffset = 2
  autoPlaceText = true
  click1_x = 211.028
  click1_y = 65.5283
  click2_x = 211.028
  click2_y = 65.5283
  comma_decimal_place = false
  dimension_line_overshoot = 1
  gap_datum_points = 0
  halfDimension_linear = false
  lineColor = rgb(255,0,0)
  strokeWidth = 0.1
  textFormat_linear = %(value)3.3f
  textRenderer_color = rgb(0,0,0)
  textRenderer_family = inherit
  textRenderer_size = 3.6
  unit_custom_scale = 1
  unit_scheme = 0
FEATURE [Drawing::FeatureViewPython] dim025  # drawing view (typed FeaturePython)
  Rotation = 0
  ViewResult = <g> \n  <line x1="211.875000" y1="73.180175" x2="205.285661" y2="73.180175" style="stroke:rgb(255,0,0);stroke-width:0.10" />\n<line x1="211.875000" y1="89.845475" x2="205.285661" y2="89.845475" style="stroke:rgb(255,0,0);stroke-width:0.10" />\n<line x1="206.285661" y1="73.180175" x2="206.285661" y2="89.845475" style="stroke:rgb(255,0,0);stroke-width:0.10" /> \n  <polygon points="206.285661,89.845475 206.785661,87.845475 206.285661,87.345475 205.785661,87.845475" style="fill:rgb(255,0,0);stroke:rgb(255,0,0);stroke-width:0" /><polygon points="206.285661,73.180175 205.785661,75.180175 206.285661,75.680175 206.785661,75.180175" style="fill:rgb(255,0,0);stroke:rgb(255,0,0);stroke-width:0" /> \n  <text x="204.285661" y="81.512825" font-family="inherit" font-size="3.6" fill="rgb(0,0,0)" text-anchor="middle" transform="rotate(-90.000000 204.285661,81.512825)" >22.2</text> </g>
  Visible = false
  X = 0
  Y = 0
  arrowL1 = 2
  arrowL2 = 0.5
  arrowW = 1
  arrow_scheme = 0
  autoPlaceOffset = 2
  autoPlaceText = true
  click1_x = 206.286
  click1_y = 89.1247
  click2_x = 206.286
  click2_y = 89.1247
  comma_decimal_place = false
  dimension_line_overshoot = 1
  gap_datum_points = 0
  halfDimension_linear = false
  lineColor = rgb(255,0,0)
  strokeWidth = 0.1
  textFormat_linear = 22.2
  textRenderer_color = rgb(0,0,0)
  textRenderer_family = inherit
  textRenderer_size = 3.6
  unit_custom_scale = 1
  unit_scheme = 0
FEATURE [Drawing::FeatureViewPython] dim026  # drawing view (typed FeaturePython)
  Rotation = 0
  ViewResult = <g> \n  <line x1="95.625000" y1="73.175000" x2="95.625000" y2="114.096178" style="stroke:rgb(255,0,0);stroke-width:0.10" />\n<line x1="73.875000" y1="73.475000" x2="73.875000" y2="114.096178" style="stroke:rgb(255,0,0);stroke-width:0.10" />\n<line x1="95.625000" y1="113.096178" x2="73.875000" y2="113.096178" style="stroke:rgb(255,0,0);stroke-width:0.10" /> \n  <polygon points="73.875000,113.096178 75.875000,113.596178 76.375000,113.096178 75.875000,112.596178" style="fill:rgb(255,0,0);stroke:rgb(255,0,0);stroke-width:0" /><polygon points="95.625000,113.096178 93.625000,112.596178 93.125000,113.096178 93.625000,113.596178" style="fill:rgb(255,0,0);stroke:rgb(255,0,0);stroke-width:0" /> \n  <text x="84.750000" y="111.096178" font-family="inherit" font-size="3.6" fill="rgb(0,0,0)" text-anchor="middle" transform="rotate(0.000000 84.750000,111.096178)" >29</text> </g>
  Visible = false
  X = 0
  Y = 0
  arrowL1 = 2
  arrowL2 = 0.5
  arrowW = 1
  arrow_scheme = 0
  autoPlaceOffset = 2
  autoPlaceText = true
  click1_x = 76.8528
  click1_y = 113.096
  click2_x = 76.8528
  click2_y = 113.096
  comma_decimal_place = false
  dimension_line_overshoot = 1
  gap_datum_points = 0
  halfDimension_linear = false
  lineColor = rgb(255,0,0)
  strokeWidth = 0.1
  textFormat_linear = %(value)3.3f
  textRenderer_color = rgb(0,0,0)
  textRenderer_family = inherit
  textRenderer_size = 3.6
  unit_custom_scale = 1
  unit_scheme = 0
FEATURE [Drawing::FeatureViewPython] dim027  # drawing view (typed FeaturePython)
  Rotation = 0
  ViewResult = <g> \n  <line x1="73.875000" y1="90.875000" x2="73.875000" y2="105.879186" style="stroke:rgb(255,0,0);stroke-width:0.10" />\n<line x1="94.200000" y1="88.625000" x2="94.200000" y2="105.879186" style="stroke:rgb(255,0,0);stroke-width:0.10" />\n<line x1="73.875000" y1="104.879186" x2="94.200000" y2="104.879186" style="stroke:rgb(255,0,0);stroke-width:0.10" /> \n  <polygon points="94.200000,104.879186 92.200000,104.379186 91.700000,104.879186 92.200000,105.379186" style="fill:rgb(255,0,0);stroke:rgb(255,0,0);stroke-width:0" /><polygon points="73.875000,104.879186 75.875000,105.379186 76.375000,104.879186 75.875000,104.379186" style="fill:rgb(255,0,0);stroke:rgb(255,0,0);stroke-width:0" /> \n  <text x="84.037500" y="102.879186" font-family="inherit" font-size="3.6" fill="rgb(0,0,0)" text-anchor="middle" transform="rotate(0.000000 84.037500,102.879186)" >27.1</text> </g>
  Visible = false
  X = 0
  Y = 0
  arrowL1 = 2
  arrowL2 = 0.5
  arrowW = 1
  arrow_scheme = 0
  autoPlaceOffset = 2
  autoPlaceText = true
  click1_x = 88.0333
  click1_y = 104.879
  click2_x = 88.0333
  click2_y = 104.879
  comma_decimal_place = false
  dimension_line_overshoot = 1
  gap_datum_points = 0
  halfDimension_linear = false
  lineColor = rgb(255,0,0)
  strokeWidth = 0.1
  textFormat_linear = %(value)3.3f
  textRenderer_color = rgb(0,0,0)
  textRenderer_family = inherit
  textRenderer_size = 3.6
  unit_custom_scale = 1
  unit_scheme = 0
FEATURE [Drawing::FeatureViewPython] dim028  # drawing view (typed FeaturePython)
  Rotation = 0
  ViewResult = <g> \n  <line x1="73.875000" y1="72.125000" x2="59.078123" y2="72.125000" style="stroke:rgb(255,0,0);stroke-width:0.10" />\n<line x1="73.875000" y1="90.875000" x2="59.078123" y2="90.875000" style="stroke:rgb(255,0,0);stroke-width:0.10" />\n<line x1="60.078123" y1="72.125000" x2="60.078123" y2="90.875000" style="stroke:rgb(255,0,0);stroke-width:0.10" /> \n  <polygon points="60.078123,90.875000 60.578123,88.875000 60.078123,88.375000 59.578123,88.875000" style="fill:rgb(255,0,0);stroke:rgb(255,0,0);stroke-width:0" /><polygon points="60.078123,72.125000 59.578123,74.125000 60.078123,74.625000 60.578123,74.125000" style="fill:rgb(255,0,0);stroke:rgb(255,0,0);stroke-width:0" /> \n  <text x="58.078123" y="81.500000" font-family="inherit" font-size="3.6" fill="rgb(0,0,0)" text-anchor="middle" transform="rotate(-90.000000 58.078123,81.500000)" >25</text> </g>
  Visible = false
  X = 0
  Y = 0
  arrowL1 = 2
  arrowL2 = 0.5
  arrowW = 1
  arrow_scheme = 0
  autoPlaceOffset = 2
  autoPlaceText = true
  click1_x = 60.0781
  click1_y = 90.4775
  click2_x = 60.0781
  click2_y = 90.4775
  comma_decimal_place = false
  dimension_line_overshoot = 1
  gap_datum_points = 0
  halfDimension_linear = false
  lineColor = rgb(255,0,0)
  strokeWidth = 0.1
  textFormat_linear = %(value)3.3f
  textRenderer_color = rgb(0,0,0)
  textRenderer_family = inherit
  textRenderer_size = 3.6
  unit_custom_scale = 1
  unit_scheme = 0
FEATURE [Drawing::FeatureViewPython] dim029  # drawing view (typed FeaturePython)
  Rotation = 0
  ViewResult = <g> \n  <line x1="73.875000" y1="73.475000" x2="65.027594" y2="73.475000" style="stroke:rgb(255,0,0);stroke-width:0.10" />\n<line x1="73.875000" y1="89.525000" x2="65.027594" y2="89.525000" style="stroke:rgb(255,0,0);stroke-width:0.10" />\n<line x1="66.027594" y1="73.475000" x2="66.027594" y2="89.525000" style="stroke:rgb(255,0,0);stroke-width:0.10" /> \n  <polygon points="66.027594,89.525000 66.527594,87.525000 66.027594,87.025000 65.527594,87.525000" style="fill:rgb(255,0,0);stroke:rgb(255,0,0);stroke-width:0" /><polygon points="66.027594,73.475000 65.527594,75.475000 66.027594,75.975000 66.527594,75.475000" style="fill:rgb(255,0,0);stroke:rgb(255,0,0);stroke-width:0" /> \n  <text x="64.027594" y="81.500000" font-family="inherit" font-size="3.6" fill="rgb(0,0,0)" text-anchor="middle" transform="rotate(-90.000000 64.027594,81.500000)" >21.4</text> </g>
  Visible = false
  X = 0
  Y = 0
  arrowL1 = 2
  arrowL2 = 0.5
  arrowW = 1
  arrow_scheme = 0
  autoPlaceOffset = 2
  autoPlaceText = true
  click1_x = 66.0276
  click1_y = 87.2713
  click2_x = 66.0276
  click2_y = 87.2713
  comma_decimal_place = false
  dimension_line_overshoot = 1
  gap_datum_points = 0
  halfDimension_linear = false
  lineColor = rgb(255,0,0)
  strokeWidth = 0.1
  textFormat_linear = %(value)3.3f
  textRenderer_color = rgb(0,0,0)
  textRenderer_family = inherit
  textRenderer_size = 3.6
  unit_custom_scale = 1
  unit_scheme = 0
FEATURE [Drawing::FeatureViewPython] dim030  # drawing view (typed FeaturePython)
  Rotation = 0
  ViewResult = <g> \n  <line x1="83.557500" y1="74.249532" x2="71.484573" y2="74.249532" style="stroke:rgb(255,0,0);stroke-width:0.10" />\n<line x1="84.070500" y1="88.769367" x2="71.484573" y2="88.769367" style="stroke:rgb(255,0,0);stroke-width:0.10" />\n<line x1="72.484573" y1="74.249532" x2="72.484573" y2="88.769367" style="stroke:rgb(255,0,0);stroke-width:0.10" /> \n  <polygon points="72.484573,88.769367 72.984573,86.769367 72.484573,86.269367 71.984573,86.769367" style="fill:rgb(255,0,0);stroke:rgb(255,0,0);stroke-width:0" /><polygon points="72.484573,74.249532 71.984573,76.249532 72.484573,76.749532 72.984573,76.249532" style="fill:rgb(255,0,0);stroke:rgb(255,0,0);stroke-width:0" /> \n  <text x="70.484573" y="81.509450" font-family="inherit" font-size="3.6" fill="rgb(0,0,0)" text-anchor="middle" transform="rotate(-90.000000 70.484573,81.509450)" >19.4</text> </g>
  Visible = false
  X = 0
  Y = 0
  arrowL1 = 2
  arrowL2 = 0.5
  arrowW = 1
  arrow_scheme = 0
  autoPlaceOffset = 2
  autoPlaceText = true
  click1_x = 72.4846
  click1_y = 88.4227
  click2_x = 72.4846
  click2_y = 88.4227
  comma_decimal_place = false
  dimension_line_overshoot = 1
  gap_datum_points = 0
  halfDimension_linear = false
  lineColor = rgb(255,0,0)
  strokeWidth = 0.1
  textFormat_linear = %(value)3.1f
  textRenderer_color = rgb(0,0,0)
  textRenderer_family = inherit
  textRenderer_size = 3.6
  unit_custom_scale = 1
  unit_scheme = 0
FEATURE [Drawing::FeatureViewPython] dim031  # drawing view (typed FeaturePython)
  Rotation = 0
  ViewResult = <g> \n  <line x1="95.625000" y1="88.625000" x2="103.869078" y2="88.625000" style="stroke:rgb(255,0,0);stroke-width:0.10" />\n<line x1="95.625000" y1="74.375000" x2="103.869078" y2="74.375000" style="stroke:rgb(255,0,0);stroke-width:0.10" />\n<line x1="102.869078" y1="88.625000" x2="102.869078" y2="74.375000" style="stroke:rgb(255,0,0);stroke-width:0.10" /> \n  <polygon points="102.869078,74.375000 102.369078,76.375000 102.869078,76.875000 103.369078,76.375000" style="fill:rgb(255,0,0);stroke:rgb(255,0,0);stroke-width:0" /><polygon points="102.869078,88.625000 103.369078,86.625000 102.869078,86.125000 102.369078,86.625000" style="fill:rgb(255,0,0);stroke:rgb(255,0,0);stroke-width:0" /> \n  <text x="100.869078" y="81.500000" font-family="inherit" font-size="3.6" fill="rgb(0,0,0)" text-anchor="middle" transform="rotate(-90.000000 100.869078,81.500000)" >19</text> </g>
  Visible = false
  X = 0
  Y = 0
  arrowL1 = 2
  arrowL2 = 0.5
  arrowW = 1
  arrow_scheme = 0
  autoPlaceOffset = 2
  autoPlaceText = true
  click1_x = 102.869
  click1_y = 75.7065
  click2_x = 102.869
  click2_y = 75.7065
  comma_decimal_place = false
  dimension_line_overshoot = 1
  gap_datum_points = 0
  halfDimension_linear = false
  lineColor = rgb(255,0,0)
  strokeWidth = 0.1
  textFormat_linear = %(value)3.3f
  textRenderer_color = rgb(0,0,0)
  textRenderer_family = inherit
  textRenderer_size = 3.6
  unit_custom_scale = 1
  unit_scheme = 0
FEATURE [Drawing::FeatureViewPython] dim032  # drawing view (typed FeaturePython)
  Rotation = 0
  ViewResult = <g> \n  <line x1="95.625000" y1="73.175000" x2="110.819885" y2="73.175000" style="stroke:rgb(255,0,0);stroke-width:0.10" />\n<line x1="95.625000" y1="89.825000" x2="110.819885" y2="89.825000" style="stroke:rgb(255,0,0);stroke-width:0.10" />\n<line x1="109.819885" y1="73.175000" x2="109.819885" y2="89.825000" style="stroke:rgb(255,0,0);stroke-width:0.10" /> \n  <polygon points="109.819885,89.825000 110.319885,87.825000 109.819885,87.325000 109.319885,87.825000" style="fill:rgb(255,0,0);stroke:rgb(255,0,0);stroke-width:0" /><polygon points="109.819885,73.175000 109.319885,75.175000 109.819885,75.675000 110.319885,75.175000" style="fill:rgb(255,0,0);stroke:rgb(255,0,0);stroke-width:0" /> \n  <text x="107.819885" y="81.500000" font-family="inherit" font-size="3.6" fill="rgb(0,0,0)" text-anchor="middle" transform="rotate(-90.000000 107.819885,81.500000)" >22.2</text> </g>
  Visible = false
  X = 0
  Y = 0
  arrowL1 = 2
  arrowL2 = 0.5
  arrowW = 1
  arrow_scheme = 0
  autoPlaceOffset = 2
  autoPlaceText = true
  click1_x = 109.82
  click1_y = 90.0202
  click2_x = 109.82
  click2_y = 90.0202
  comma_decimal_place = false
  dimension_line_overshoot = 1
  gap_datum_points = 0
  halfDimension_linear = false
  lineColor = rgb(255,0,0)
  strokeWidth = 0.1
  textFormat_linear = %(value)3.3f
  textRenderer_color = rgb(0,0,0)
  textRenderer_family = inherit
  textRenderer_size = 3.6
  unit_custom_scale = 1
  unit_scheme = 0
FEATURE [Drawing::FeaturePage] Page  label="BatteruHolderProjections"
  EditableTexts = Dr. Zoidberg | 13.02.2019 | x1.0 | ??? | ERG-T-01 | Battery Holder. Projections. | Part #2 | Sheet #1
  Group = -> [Ortho,Ortho023,Ortho024,dia001,dia002,dia003,dia004,dia005,dim020,dim021,dim022,dim024,dim023,dim025,dim026,dim027,dim028,dim029,dim030,dim031,dim032]
  Template = <path>
note: 4 file-system paths scrubbed to <path> (originals preserved in the JSON sidecar)
